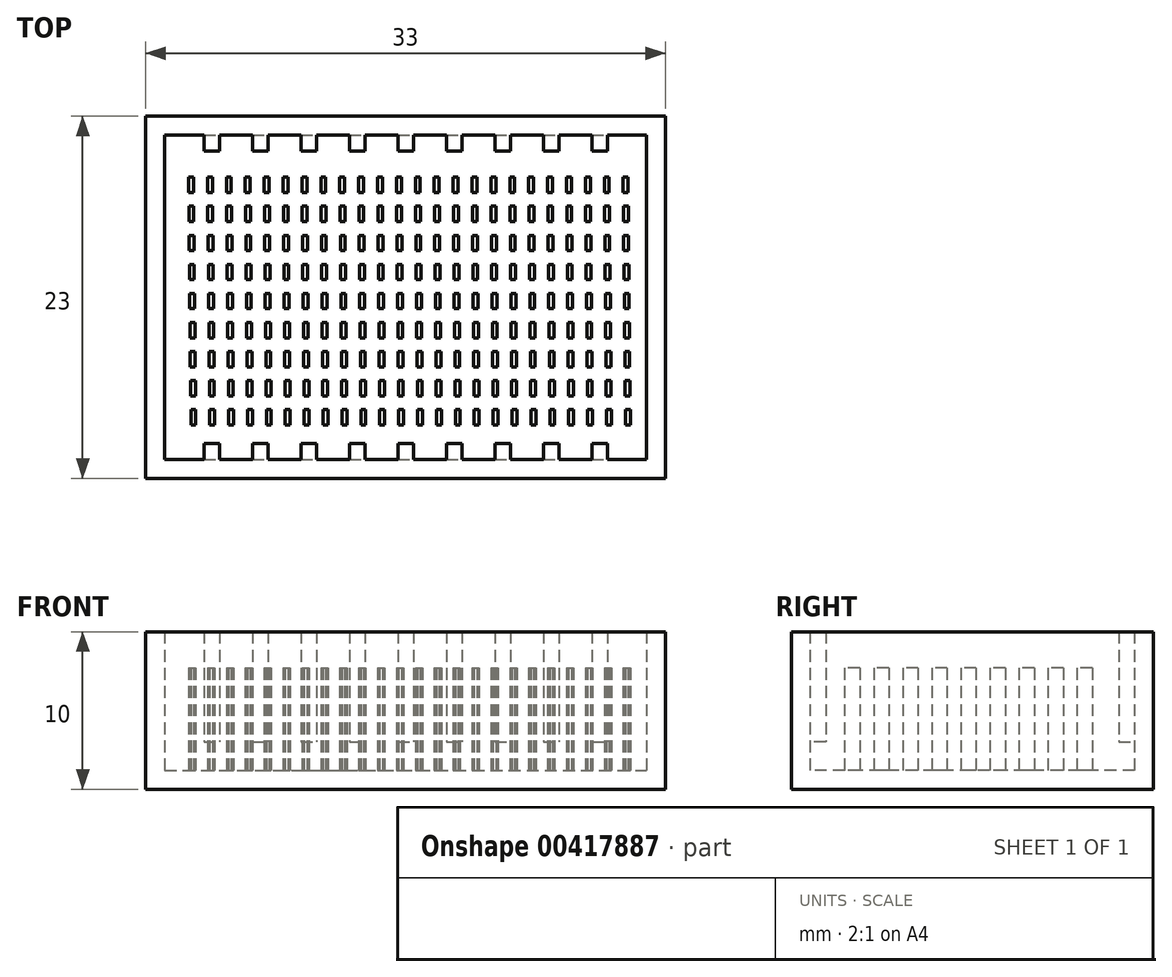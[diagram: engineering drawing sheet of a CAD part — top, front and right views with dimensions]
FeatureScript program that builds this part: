
annotation { "Feature Type Name" : "Feature", "Feature Type Description" : "" }
export const myFeature = defineFeature(function(context is Context, id is Id, definition is map)
    precondition{}
    {
        {
            var Q0;
            Q0=qCreatedBy(makeId("Top.planeOp"),FACE);
            var sketch = newSketch(context, id + "F0", { "sketchPlane" : qUnion([Q0])});
            skLineSegment(sketch, "E0.bottom", {"start": v(-104.56, 23) * mm, "end": v(-71.56, 23) * mm});
            skLineSegment(sketch, "E0.top", {"start": v(-104.56, 0) * mm, "end": v(-71.56, 0) * mm});
            skLineSegment(sketch, "E0.left", {"start": v(-104.56, 23) * mm, "end": v(-104.56, 0) * mm});
            skLineSegment(sketch, "E0.right", {"start": v(-71.56, 23) * mm, "end": v(-71.56, 0) * mm});
            skLineSegment(sketch, "E1.0", {"start": v(-103.36, 1.2) * mm, "end": v(-72.76, 1.2) * mm});
            skLineSegment(sketch, "E1.1", {"start": v(-103.36, 21.8) * mm, "end": v(-103.36, 1.2) * mm});
            skLineSegment(sketch, "E1.2", {"start": v(-103.36, 21.8) * mm, "end": v(-72.76, 21.8) * mm});
            skLineSegment(sketch, "E1.3", {"start": v(-72.76, 21.8) * mm, "end": v(-72.76, 1.2) * mm});
            skSolve(sketch);
        }
        {
            var Q0;
            Q0=makeQuery(id+"F0.imprint","IMPRINT",FACE,{"disambiguationData":[TD([[makeQuery(id+"F0.imprint","IMPRINT",EDGE,{"derivedFrom":sQuery(id+"F0.wireOp",EDGE,"E0.bottom")}),-1.0]])]});
            extrude(context, id + "F1", {"entities" : qUnion([Q0]), "depth" : 10 * mm});
        }
        {
            var Q0;
            Q0=makeQuery(id+"F0.imprint","IMPRINT",FACE,{"disambiguationData":[TD([[makeQuery(id+"F0.imprint","IMPRINT",EDGE,{"derivedFrom":sQuery(id+"F0.wireOp",EDGE,"E1.0")}),1.0]])]});
            extrude(context, id + "F2", {"entities" : qUnion([Q0]), "operationType" : NewBodyOperationType.ADD, "depth" : 1.2 * mm});
        }
        {
            var Q0;
            Q0=makeQuery(id+"F1.opExtrude","SWEPT_FACE",FACE,{"disambiguationData":[OSD([sQuery(id+"F0.wireOp",EDGE,"E1.2")])]});
            var sketch = newSketch(context, id + "F3", { "sketchPlane" : qUnion([Q0])});
            skLineSegment(sketch, "E2.bottom", {"start": v(-100.87, 10) * mm, "end": v(-99.87, 10) * mm});
            skLineSegment(sketch, "E2.top", {"start": v(-100.87, 3) * mm, "end": v(-99.87, 3) * mm});
            skLineSegment(sketch, "E2.left", {"start": v(-100.87, 10) * mm, "end": v(-100.87, 3) * mm});
            skLineSegment(sketch, "E2.right", {"start": v(-99.87, 10) * mm, "end": v(-99.87, 3) * mm});
            skLineSegment(sketch, "E3.1.0.0", {"start": v(-97.79, 10) * mm, "end": v(-96.79, 10) * mm});
            skLineSegment(sketch, "E3.1.0.1", {"start": v(-96.79, 10) * mm, "end": v(-96.79, 3) * mm});
            skLineSegment(sketch, "E3.1.0.2", {"start": v(-97.79, 10) * mm, "end": v(-97.79, 3) * mm});
            skLineSegment(sketch, "E3.1.0.3", {"start": v(-97.79, 3) * mm, "end": v(-96.79, 3) * mm});
            skLineSegment(sketch, "E3.2.0.0", {"start": v(-94.7, 10) * mm, "end": v(-93.7, 10) * mm});
            skLineSegment(sketch, "E3.2.0.1", {"start": v(-93.7, 10) * mm, "end": v(-93.7, 3) * mm});
            skLineSegment(sketch, "E3.2.0.2", {"start": v(-94.7, 10) * mm, "end": v(-94.7, 3) * mm});
            skLineSegment(sketch, "E3.2.0.3", {"start": v(-94.7, 3) * mm, "end": v(-93.7, 3) * mm});
            skLineSegment(sketch, "E3.3.0.0", {"start": v(-91.63, 10) * mm, "end": v(-90.63, 10) * mm});
            skLineSegment(sketch, "E3.3.0.1", {"start": v(-90.63, 10) * mm, "end": v(-90.63, 3) * mm});
            skLineSegment(sketch, "E3.3.0.2", {"start": v(-91.63, 10) * mm, "end": v(-91.63, 3) * mm});
            skLineSegment(sketch, "E3.3.0.3", {"start": v(-91.63, 3) * mm, "end": v(-90.63, 3) * mm});
            skLineSegment(sketch, "E3.4.0.0", {"start": v(-88.55, 10) * mm, "end": v(-87.55, 10) * mm});
            skLineSegment(sketch, "E3.4.0.1", {"start": v(-87.55, 10) * mm, "end": v(-87.55, 3) * mm});
            skLineSegment(sketch, "E3.4.0.2", {"start": v(-88.55, 10) * mm, "end": v(-88.55, 3) * mm});
            skLineSegment(sketch, "E3.4.0.3", {"start": v(-88.55, 3) * mm, "end": v(-87.55, 3) * mm});
            skLineSegment(sketch, "E3.5.0.0", {"start": v(-85.47, 10) * mm, "end": v(-84.47, 10) * mm});
            skLineSegment(sketch, "E3.5.0.1", {"start": v(-84.47, 10) * mm, "end": v(-84.47, 3) * mm});
            skLineSegment(sketch, "E3.5.0.2", {"start": v(-85.47, 10) * mm, "end": v(-85.47, 3) * mm});
            skLineSegment(sketch, "E3.5.0.3", {"start": v(-85.47, 3) * mm, "end": v(-84.47, 3) * mm});
            skLineSegment(sketch, "E3.6.0.0", {"start": v(-82.39, 10) * mm, "end": v(-81.39, 10) * mm});
            skLineSegment(sketch, "E3.6.0.1", {"start": v(-81.39, 10) * mm, "end": v(-81.39, 3) * mm});
            skLineSegment(sketch, "E3.6.0.2", {"start": v(-82.39, 10) * mm, "end": v(-82.39, 3) * mm});
            skLineSegment(sketch, "E3.6.0.3", {"start": v(-82.39, 3) * mm, "end": v(-81.39, 3) * mm});
            skLineSegment(sketch, "E3.7.0.0", {"start": v(-79.3, 10) * mm, "end": v(-78.3, 10) * mm});
            skLineSegment(sketch, "E3.7.0.1", {"start": v(-78.3, 10) * mm, "end": v(-78.3, 3) * mm});
            skLineSegment(sketch, "E3.7.0.2", {"start": v(-79.3, 10) * mm, "end": v(-79.3, 3) * mm});
            skLineSegment(sketch, "E3.7.0.3", {"start": v(-79.3, 3) * mm, "end": v(-78.3, 3) * mm});
            skLineSegment(sketch, "E3.8.0.0", {"start": v(-76.23, 10) * mm, "end": v(-75.23, 10) * mm});
            skLineSegment(sketch, "E3.8.0.1", {"start": v(-75.23, 10) * mm, "end": v(-75.23, 3) * mm});
            skLineSegment(sketch, "E3.8.0.2", {"start": v(-76.23, 10) * mm, "end": v(-76.23, 3) * mm});
            skLineSegment(sketch, "E3.8.0.3", {"start": v(-76.23, 3) * mm, "end": v(-75.23, 3) * mm});
            skLineSegment(sketch, "E3.direction1", {"start": v(-100.87, 10) * mm, "end": v(-97.79, 10) * mm, "construction": true});
            skSolve(sketch);
        }
        {
            var Q0;
            Q0=makeQuery(id+"F3.imprint","IMPRINT",FACE,{"disambiguationData":[TD([[makeQuery(id+"F3.imprint","IMPRINT",EDGE,{"derivedFrom":sQuery(id+"F3.wireOp",EDGE,"E3.1.0.0")}),-1.0]])]});
            var Q1;
            Q1=makeQuery(id+"F3.imprint","IMPRINT",FACE,{"disambiguationData":[TD([[makeQuery(id+"F3.imprint","IMPRINT",EDGE,{"derivedFrom":sQuery(id+"F3.wireOp",EDGE,"E3.2.0.0")}),-1.0]])]});
            var Q2;
            Q2=makeQuery(id+"F3.imprint","IMPRINT",FACE,{"disambiguationData":[TD([[makeQuery(id+"F3.imprint","IMPRINT",EDGE,{"derivedFrom":sQuery(id+"F3.wireOp",EDGE,"E3.3.0.0")}),-1.0]])]});
            var Q3;
            Q3=makeQuery(id+"F3.imprint","IMPRINT",FACE,{"disambiguationData":[TD([[makeQuery(id+"F3.imprint","IMPRINT",EDGE,{"derivedFrom":sQuery(id+"F3.wireOp",EDGE,"E3.4.0.0")}),-1.0]])]});
            var Q4;
            Q4=makeQuery(id+"F3.imprint","IMPRINT",FACE,{"disambiguationData":[TD([[makeQuery(id+"F3.imprint","IMPRINT",EDGE,{"derivedFrom":sQuery(id+"F3.wireOp",EDGE,"E3.5.0.0")}),-1.0]])]});
            var Q5;
            Q5=makeQuery(id+"F3.imprint","IMPRINT",FACE,{"disambiguationData":[TD([[makeQuery(id+"F3.imprint","IMPRINT",EDGE,{"derivedFrom":sQuery(id+"F3.wireOp",EDGE,"E3.6.0.0")}),-1.0]])]});
            var Q6;
            Q6=makeQuery(id+"F3.imprint","IMPRINT",FACE,{"disambiguationData":[TD([[makeQuery(id+"F3.imprint","IMPRINT",EDGE,{"derivedFrom":sQuery(id+"F3.wireOp",EDGE,"E3.7.0.0")}),-1.0]])]});
            var Q7;
            Q7=makeQuery(id+"F3.imprint","IMPRINT",FACE,{"disambiguationData":[TD([[makeQuery(id+"F3.imprint","IMPRINT",EDGE,{"derivedFrom":sQuery(id+"F3.wireOp",EDGE,"E3.8.0.0")}),-1.0]])]});
            var Q8;
            Q8=makeQuery(id+"F3.imprint","IMPRINT",FACE,{"disambiguationData":[TD([[makeQuery(id+"F3.imprint","IMPRINT",EDGE,{"derivedFrom":sQuery(id+"F3.wireOp",EDGE,"E2.bottom")}),-1.0]])]});
            extrude(context, id + "F4", {"entities" : qUnion([Q0, Q1, Q2, Q3, Q4, Q5, Q6, Q7, Q8]), "operationType" : NewBodyOperationType.ADD, "depth" : 1 * mm});
        }
        {
            var Q0;
            Q0=makeQuery(id+"F1.opExtrude","SWEPT_FACE",FACE,{"disambiguationData":[OSD([sQuery(id+"F0.wireOp",EDGE,"E1.0")])]});
            var sketch = newSketch(context, id + "F5", { "sketchPlane" : qUnion([Q0])});
            skLineSegment(sketch, "E4.0", {"start": v(76.23, 10) * mm, "end": v(75.23, 10) * mm});
            skLineSegment(sketch, "E4.1", {"start": v(76.23, 10) * mm, "end": v(76.23, 3) * mm});
            skLineSegment(sketch, "E4.2", {"start": v(75.23, 10) * mm, "end": v(75.23, 3) * mm});
            skLineSegment(sketch, "E4.3", {"start": v(76.23, 3) * mm, "end": v(75.23, 3) * mm});
            skLineSegment(sketch, "E4.4", {"start": v(79.3, 3) * mm, "end": v(78.3, 3) * mm});
            skLineSegment(sketch, "E4.5", {"start": v(79.3, 10) * mm, "end": v(79.3, 3) * mm});
            skLineSegment(sketch, "E4.6", {"start": v(78.3, 10) * mm, "end": v(78.3, 3) * mm});
            skLineSegment(sketch, "E4.7", {"start": v(79.3, 10) * mm, "end": v(78.3, 10) * mm});
            skLineSegment(sketch, "E4.8", {"start": v(82.39, 10) * mm, "end": v(81.39, 10) * mm});
            skLineSegment(sketch, "E4.9", {"start": v(81.39, 10) * mm, "end": v(81.39, 3) * mm});
            skLineSegment(sketch, "E4.10", {"start": v(82.39, 10) * mm, "end": v(82.39, 3) * mm});
            skLineSegment(sketch, "E4.11", {"start": v(82.39, 3) * mm, "end": v(81.39, 3) * mm});
            skLineSegment(sketch, "E4.12", {"start": v(85.47, 3) * mm, "end": v(84.47, 3) * mm});
            skLineSegment(sketch, "E4.13", {"start": v(85.47, 10) * mm, "end": v(85.47, 3) * mm});
            skLineSegment(sketch, "E4.14", {"start": v(84.47, 10) * mm, "end": v(84.47, 3) * mm});
            skLineSegment(sketch, "E4.15", {"start": v(85.47, 10) * mm, "end": v(84.47, 10) * mm});
            skLineSegment(sketch, "E4.16", {"start": v(87.55, 10) * mm, "end": v(87.55, 3) * mm});
            skLineSegment(sketch, "E4.17", {"start": v(88.55, 10) * mm, "end": v(88.55, 3) * mm});
            skLineSegment(sketch, "E4.18", {"start": v(88.55, 10) * mm, "end": v(87.55, 10) * mm});
            skLineSegment(sketch, "E4.19", {"start": v(88.55, 3) * mm, "end": v(87.55, 3) * mm});
            skLineSegment(sketch, "E4.20", {"start": v(91.63, 3) * mm, "end": v(90.63, 3) * mm});
            skLineSegment(sketch, "E4.21", {"start": v(90.63, 10) * mm, "end": v(90.63, 3) * mm});
            skLineSegment(sketch, "E4.22", {"start": v(91.63, 10) * mm, "end": v(91.63, 3) * mm});
            skLineSegment(sketch, "E4.23", {"start": v(91.63, 10) * mm, "end": v(90.63, 10) * mm});
            skLineSegment(sketch, "E4.24", {"start": v(94.7, 10) * mm, "end": v(93.7, 10) * mm});
            skLineSegment(sketch, "E4.25", {"start": v(93.7, 10) * mm, "end": v(93.7, 3) * mm});
            skLineSegment(sketch, "E4.26", {"start": v(94.7, 10) * mm, "end": v(94.7, 3) * mm});
            skLineSegment(sketch, "E4.27", {"start": v(94.7, 3) * mm, "end": v(93.7, 3) * mm});
            skLineSegment(sketch, "E4.28", {"start": v(96.79, 10) * mm, "end": v(96.79, 3) * mm});
            skLineSegment(sketch, "E4.29", {"start": v(97.79, 10) * mm, "end": v(97.79, 3) * mm});
            skLineSegment(sketch, "E4.30", {"start": v(97.79, 10) * mm, "end": v(96.79, 10) * mm});
            skLineSegment(sketch, "E4.31", {"start": v(97.79, 3) * mm, "end": v(96.79, 3) * mm});
            skLineSegment(sketch, "E4.32", {"start": v(100.87, 3) * mm, "end": v(99.87, 3) * mm});
            skLineSegment(sketch, "E4.33", {"start": v(100.87, 10) * mm, "end": v(100.87, 3) * mm});
            skLineSegment(sketch, "E4.34", {"start": v(99.87, 10) * mm, "end": v(99.87, 3) * mm});
            skLineSegment(sketch, "E4.35", {"start": v(100.87, 10) * mm, "end": v(99.87, 10) * mm});
            skSolve(sketch);
        }
        {
            var Q0;
            Q0=makeQuery(id+"F5.imprint","IMPRINT",FACE,{"disambiguationData":[TD([[makeQuery(id+"F5.imprint","IMPRINT",EDGE,{"derivedFrom":sQuery(id+"F5.wireOp",EDGE,"E4.0")}),1.0]])]});
            var Q1;
            Q1=makeQuery(id+"F5.imprint","IMPRINT",FACE,{"disambiguationData":[TD([[makeQuery(id+"F5.imprint","IMPRINT",EDGE,{"derivedFrom":sQuery(id+"F5.wireOp",EDGE,"E4.4")}),-1.0]])]});
            var Q2;
            Q2=makeQuery(id+"F5.imprint","IMPRINT",FACE,{"disambiguationData":[TD([[makeQuery(id+"F5.imprint","IMPRINT",EDGE,{"derivedFrom":sQuery(id+"F5.wireOp",EDGE,"E4.8")}),1.0]])]});
            var Q3;
            Q3=makeQuery(id+"F5.imprint","IMPRINT",FACE,{"disambiguationData":[TD([[makeQuery(id+"F5.imprint","IMPRINT",EDGE,{"derivedFrom":sQuery(id+"F5.wireOp",EDGE,"E4.12")}),-1.0]])]});
            var Q4;
            Q4=makeQuery(id+"F5.imprint","IMPRINT",FACE,{"disambiguationData":[TD([[makeQuery(id+"F5.imprint","IMPRINT",EDGE,{"derivedFrom":sQuery(id+"F5.wireOp",EDGE,"E4.16")}),1.0]])]});
            var Q5;
            Q5=makeQuery(id+"F5.imprint","IMPRINT",FACE,{"disambiguationData":[TD([[makeQuery(id+"F5.imprint","IMPRINT",EDGE,{"derivedFrom":sQuery(id+"F5.wireOp",EDGE,"E4.20")}),-1.0]])]});
            var Q6;
            Q6=makeQuery(id+"F5.imprint","IMPRINT",FACE,{"disambiguationData":[TD([[makeQuery(id+"F5.imprint","IMPRINT",EDGE,{"derivedFrom":sQuery(id+"F5.wireOp",EDGE,"E4.24")}),1.0]])]});
            var Q7;
            Q7=makeQuery(id+"F5.imprint","IMPRINT",FACE,{"disambiguationData":[TD([[makeQuery(id+"F5.imprint","IMPRINT",EDGE,{"derivedFrom":sQuery(id+"F5.wireOp",EDGE,"E4.28")}),1.0]])]});
            var Q8;
            Q8=makeQuery(id+"F5.imprint","IMPRINT",FACE,{"disambiguationData":[TD([[makeQuery(id+"F5.imprint","IMPRINT",EDGE,{"derivedFrom":sQuery(id+"F5.wireOp",EDGE,"E4.32")}),-1.0]])]});
            extrude(context, id + "F6", {"entities" : qUnion([Q0, Q1, Q2, Q3, Q4, Q5, Q6, Q7, Q8]), "operationType" : NewBodyOperationType.ADD, "depth" : 1 * mm});
        }
        {
            var Q0;
            Q0=makeQuery(id+"F2.opExtrude","CAP_FACE",FACE,{"disambiguationData":[OSD([sQuery(id+"F0.wireOp",EDGE,"E1.0"),sQuery(id+"F0.wireOp",EDGE,"E1.1"),sQuery(id+"F0.wireOp",EDGE,"E1.2"),sQuery(id+"F0.wireOp",EDGE,"E1.3")])],"isStart":false});
            var sketch = newSketch(context, id + "F7", { "sketchPlane" : qUnion([Q0])});
            skLineSegment(sketch, "E5.bottom", {"start": v(-101.84, 19.12) * mm, "end": v(-101.53, 19.12) * mm});
            skLineSegment(sketch, "E5.top", {"start": v(-101.84, 18.16) * mm, "end": v(-101.53, 18.16) * mm});
            skLineSegment(sketch, "E5.left", {"start": v(-101.84, 19.12) * mm, "end": v(-101.84, 18.16) * mm});
            skLineSegment(sketch, "E5.right", {"start": v(-101.53, 19.12) * mm, "end": v(-101.53, 18.16) * mm});
            skLineSegment(sketch, "E6.1.0.0", {"start": v(-100.64, 19.12) * mm, "end": v(-100.33, 19.12) * mm});
            skLineSegment(sketch, "E6.1.0.1", {"start": v(-100.64, 18.16) * mm, "end": v(-100.33, 18.16) * mm});
            skLineSegment(sketch, "E6.1.0.2", {"start": v(-100.64, 19.12) * mm, "end": v(-100.64, 18.16) * mm});
            skLineSegment(sketch, "E6.1.0.3", {"start": v(-100.33, 19.12) * mm, "end": v(-100.33, 18.16) * mm});
            skLineSegment(sketch, "E6.2.0.0", {"start": v(-99.44, 19.12) * mm, "end": v(-99.13, 19.12) * mm});
            skLineSegment(sketch, "E6.2.0.1", {"start": v(-99.44, 18.16) * mm, "end": v(-99.13, 18.16) * mm});
            skLineSegment(sketch, "E6.2.0.2", {"start": v(-99.44, 19.12) * mm, "end": v(-99.44, 18.16) * mm});
            skLineSegment(sketch, "E6.2.0.3", {"start": v(-99.13, 19.12) * mm, "end": v(-99.13, 18.16) * mm});
            skLineSegment(sketch, "E6.3.0.0", {"start": v(-98.24, 19.12) * mm, "end": v(-97.93, 19.12) * mm});
            skLineSegment(sketch, "E6.3.0.1", {"start": v(-98.24, 18.16) * mm, "end": v(-97.93, 18.16) * mm});
            skLineSegment(sketch, "E6.3.0.2", {"start": v(-98.24, 19.12) * mm, "end": v(-98.24, 18.16) * mm});
            skLineSegment(sketch, "E6.3.0.3", {"start": v(-97.93, 19.12) * mm, "end": v(-97.93, 18.16) * mm});
            skLineSegment(sketch, "E6.4.0.0", {"start": v(-97.04, 19.12) * mm, "end": v(-96.73, 19.12) * mm});
            skLineSegment(sketch, "E6.4.0.1", {"start": v(-97.04, 18.16) * mm, "end": v(-96.73, 18.16) * mm});
            skLineSegment(sketch, "E6.4.0.2", {"start": v(-97.04, 19.12) * mm, "end": v(-97.04, 18.16) * mm});
            skLineSegment(sketch, "E6.4.0.3", {"start": v(-96.73, 19.12) * mm, "end": v(-96.73, 18.16) * mm});
            skLineSegment(sketch, "E6.5.0.0", {"start": v(-95.84, 19.12) * mm, "end": v(-95.53, 19.12) * mm});
            skLineSegment(sketch, "E6.5.0.1", {"start": v(-95.84, 18.16) * mm, "end": v(-95.53, 18.16) * mm});
            skLineSegment(sketch, "E6.5.0.2", {"start": v(-95.84, 19.12) * mm, "end": v(-95.84, 18.16) * mm});
            skLineSegment(sketch, "E6.5.0.3", {"start": v(-95.53, 19.12) * mm, "end": v(-95.53, 18.16) * mm});
            skLineSegment(sketch, "E6.6.0.0", {"start": v(-94.64, 19.12) * mm, "end": v(-94.33, 19.12) * mm});
            skLineSegment(sketch, "E6.6.0.1", {"start": v(-94.64, 18.16) * mm, "end": v(-94.33, 18.16) * mm});
            skLineSegment(sketch, "E6.6.0.2", {"start": v(-94.64, 19.12) * mm, "end": v(-94.64, 18.16) * mm});
            skLineSegment(sketch, "E6.6.0.3", {"start": v(-94.33, 19.12) * mm, "end": v(-94.33, 18.16) * mm});
            skLineSegment(sketch, "E6.7.0.0", {"start": v(-93.44, 19.12) * mm, "end": v(-93.13, 19.12) * mm});
            skLineSegment(sketch, "E6.7.0.1", {"start": v(-93.44, 18.16) * mm, "end": v(-93.13, 18.16) * mm});
            skLineSegment(sketch, "E6.7.0.2", {"start": v(-93.44, 19.12) * mm, "end": v(-93.44, 18.16) * mm});
            skLineSegment(sketch, "E6.7.0.3", {"start": v(-93.13, 19.12) * mm, "end": v(-93.13, 18.16) * mm});
            skLineSegment(sketch, "E6.8.0.0", {"start": v(-92.24, 19.12) * mm, "end": v(-91.93, 19.12) * mm});
            skLineSegment(sketch, "E6.8.0.1", {"start": v(-92.24, 18.16) * mm, "end": v(-91.93, 18.16) * mm});
            skLineSegment(sketch, "E6.8.0.2", {"start": v(-92.24, 19.12) * mm, "end": v(-92.24, 18.16) * mm});
            skLineSegment(sketch, "E6.8.0.3", {"start": v(-91.93, 19.12) * mm, "end": v(-91.93, 18.16) * mm});
            skLineSegment(sketch, "E6.9.0.0", {"start": v(-91.04, 19.12) * mm, "end": v(-90.73, 19.12) * mm});
            skLineSegment(sketch, "E6.9.0.1", {"start": v(-91.04, 18.16) * mm, "end": v(-90.73, 18.16) * mm});
            skLineSegment(sketch, "E6.9.0.2", {"start": v(-91.04, 19.12) * mm, "end": v(-91.04, 18.16) * mm});
            skLineSegment(sketch, "E6.9.0.3", {"start": v(-90.73, 19.12) * mm, "end": v(-90.73, 18.16) * mm});
            skLineSegment(sketch, "E6.10.0.0", {"start": v(-89.84, 19.12) * mm, "end": v(-89.53, 19.12) * mm});
            skLineSegment(sketch, "E6.10.0.1", {"start": v(-89.84, 18.16) * mm, "end": v(-89.53, 18.16) * mm});
            skLineSegment(sketch, "E6.10.0.2", {"start": v(-89.84, 19.12) * mm, "end": v(-89.84, 18.16) * mm});
            skLineSegment(sketch, "E6.10.0.3", {"start": v(-89.53, 19.12) * mm, "end": v(-89.53, 18.16) * mm});
            skLineSegment(sketch, "E6.11.0.0", {"start": v(-88.64, 19.12) * mm, "end": v(-88.33, 19.12) * mm});
            skLineSegment(sketch, "E6.11.0.1", {"start": v(-88.64, 18.16) * mm, "end": v(-88.33, 18.16) * mm});
            skLineSegment(sketch, "E6.11.0.2", {"start": v(-88.64, 19.12) * mm, "end": v(-88.64, 18.16) * mm});
            skLineSegment(sketch, "E6.11.0.3", {"start": v(-88.33, 19.12) * mm, "end": v(-88.33, 18.16) * mm});
            skLineSegment(sketch, "E6.12.0.0", {"start": v(-87.44, 19.12) * mm, "end": v(-87.13, 19.12) * mm});
            skLineSegment(sketch, "E6.12.0.1", {"start": v(-87.44, 18.16) * mm, "end": v(-87.13, 18.16) * mm});
            skLineSegment(sketch, "E6.12.0.2", {"start": v(-87.44, 19.12) * mm, "end": v(-87.44, 18.16) * mm});
            skLineSegment(sketch, "E6.12.0.3", {"start": v(-87.13, 19.12) * mm, "end": v(-87.13, 18.16) * mm});
            skLineSegment(sketch, "E6.13.0.0", {"start": v(-86.24, 19.12) * mm, "end": v(-85.93, 19.12) * mm});
            skLineSegment(sketch, "E6.13.0.1", {"start": v(-86.24, 18.16) * mm, "end": v(-85.93, 18.16) * mm});
            skLineSegment(sketch, "E6.13.0.2", {"start": v(-86.24, 19.12) * mm, "end": v(-86.24, 18.16) * mm});
            skLineSegment(sketch, "E6.13.0.3", {"start": v(-85.93, 19.12) * mm, "end": v(-85.93, 18.16) * mm});
            skLineSegment(sketch, "E6.14.0.0", {"start": v(-85.04, 19.12) * mm, "end": v(-84.73, 19.12) * mm});
            skLineSegment(sketch, "E6.14.0.1", {"start": v(-85.04, 18.16) * mm, "end": v(-84.73, 18.16) * mm});
            skLineSegment(sketch, "E6.14.0.2", {"start": v(-85.04, 19.12) * mm, "end": v(-85.04, 18.16) * mm});
            skLineSegment(sketch, "E6.14.0.3", {"start": v(-84.73, 19.12) * mm, "end": v(-84.73, 18.16) * mm});
            skLineSegment(sketch, "E6.15.0.0", {"start": v(-83.84, 19.12) * mm, "end": v(-83.53, 19.12) * mm});
            skLineSegment(sketch, "E6.15.0.1", {"start": v(-83.84, 18.16) * mm, "end": v(-83.53, 18.16) * mm});
            skLineSegment(sketch, "E6.15.0.2", {"start": v(-83.84, 19.12) * mm, "end": v(-83.84, 18.16) * mm});
            skLineSegment(sketch, "E6.15.0.3", {"start": v(-83.53, 19.12) * mm, "end": v(-83.53, 18.16) * mm});
            skLineSegment(sketch, "E6.16.0.0", {"start": v(-82.64, 19.12) * mm, "end": v(-82.33, 19.12) * mm});
            skLineSegment(sketch, "E6.16.0.1", {"start": v(-82.64, 18.16) * mm, "end": v(-82.33, 18.16) * mm});
            skLineSegment(sketch, "E6.16.0.2", {"start": v(-82.64, 19.12) * mm, "end": v(-82.64, 18.16) * mm});
            skLineSegment(sketch, "E6.16.0.3", {"start": v(-82.33, 19.12) * mm, "end": v(-82.33, 18.16) * mm});
            skLineSegment(sketch, "E6.17.0.0", {"start": v(-81.44, 19.12) * mm, "end": v(-81.13, 19.12) * mm});
            skLineSegment(sketch, "E6.17.0.1", {"start": v(-81.44, 18.16) * mm, "end": v(-81.13, 18.16) * mm});
            skLineSegment(sketch, "E6.17.0.2", {"start": v(-81.44, 19.12) * mm, "end": v(-81.44, 18.16) * mm});
            skLineSegment(sketch, "E6.17.0.3", {"start": v(-81.13, 19.12) * mm, "end": v(-81.13, 18.16) * mm});
            skLineSegment(sketch, "E6.18.0.0", {"start": v(-80.24, 19.12) * mm, "end": v(-79.93, 19.12) * mm});
            skLineSegment(sketch, "E6.18.0.1", {"start": v(-80.24, 18.16) * mm, "end": v(-79.93, 18.16) * mm});
            skLineSegment(sketch, "E6.18.0.2", {"start": v(-80.24, 19.12) * mm, "end": v(-80.24, 18.16) * mm});
            skLineSegment(sketch, "E6.18.0.3", {"start": v(-79.93, 19.12) * mm, "end": v(-79.93, 18.16) * mm});
            skLineSegment(sketch, "E6.19.0.0", {"start": v(-79.04, 19.12) * mm, "end": v(-78.73, 19.12) * mm});
            skLineSegment(sketch, "E6.19.0.1", {"start": v(-79.04, 18.16) * mm, "end": v(-78.73, 18.16) * mm});
            skLineSegment(sketch, "E6.19.0.2", {"start": v(-79.04, 19.12) * mm, "end": v(-79.04, 18.16) * mm});
            skLineSegment(sketch, "E6.19.0.3", {"start": v(-78.73, 19.12) * mm, "end": v(-78.73, 18.16) * mm});
            skLineSegment(sketch, "E6.20.0.0", {"start": v(-77.84, 19.12) * mm, "end": v(-77.53, 19.12) * mm});
            skLineSegment(sketch, "E6.20.0.1", {"start": v(-77.84, 18.16) * mm, "end": v(-77.53, 18.16) * mm});
            skLineSegment(sketch, "E6.20.0.2", {"start": v(-77.84, 19.12) * mm, "end": v(-77.84, 18.16) * mm});
            skLineSegment(sketch, "E6.20.0.3", {"start": v(-77.53, 19.12) * mm, "end": v(-77.53, 18.16) * mm});
            skLineSegment(sketch, "E6.21.0.0", {"start": v(-76.64, 19.12) * mm, "end": v(-76.33, 19.12) * mm});
            skLineSegment(sketch, "E6.21.0.1", {"start": v(-76.64, 18.16) * mm, "end": v(-76.33, 18.16) * mm});
            skLineSegment(sketch, "E6.21.0.2", {"start": v(-76.64, 19.12) * mm, "end": v(-76.64, 18.16) * mm});
            skLineSegment(sketch, "E6.21.0.3", {"start": v(-76.33, 19.12) * mm, "end": v(-76.33, 18.16) * mm});
            skLineSegment(sketch, "E6.22.0.0", {"start": v(-75.44, 19.12) * mm, "end": v(-75.13, 19.12) * mm});
            skLineSegment(sketch, "E6.22.0.1", {"start": v(-75.44, 18.16) * mm, "end": v(-75.13, 18.16) * mm});
            skLineSegment(sketch, "E6.22.0.2", {"start": v(-75.44, 19.12) * mm, "end": v(-75.44, 18.16) * mm});
            skLineSegment(sketch, "E6.22.0.3", {"start": v(-75.13, 19.12) * mm, "end": v(-75.13, 18.16) * mm});
            skLineSegment(sketch, "E6.23.0.0", {"start": v(-74.24, 19.12) * mm, "end": v(-73.93, 19.12) * mm});
            skLineSegment(sketch, "E6.23.0.1", {"start": v(-74.24, 18.16) * mm, "end": v(-73.93, 18.16) * mm});
            skLineSegment(sketch, "E6.23.0.2", {"start": v(-74.24, 19.12) * mm, "end": v(-74.24, 18.16) * mm});
            skLineSegment(sketch, "E6.23.0.3", {"start": v(-73.93, 19.12) * mm, "end": v(-73.93, 18.16) * mm});
            skLineSegment(sketch, "E6.direction1", {"start": v(-101.84, 18.16) * mm, "end": v(-100.64, 18.16) * mm, "construction": true});
            skLineSegment(sketch, "E7.1.0.0", {"start": v(-101.82, 17.28) * mm, "end": v(-101.82, 16.31) * mm});
            skLineSegment(sketch, "E7.1.0.1", {"start": v(-101.5, 17.28) * mm, "end": v(-101.5, 16.31) * mm});
            skLineSegment(sketch, "E7.1.0.2", {"start": v(-99.42, 17.28) * mm, "end": v(-99.42, 16.31) * mm});
            skLineSegment(sketch, "E7.1.0.3", {"start": v(-99.1, 17.28) * mm, "end": v(-99.1, 16.31) * mm});
            skLineSegment(sketch, "E7.1.0.4", {"start": v(-75.42, 17.28) * mm, "end": v(-75.1, 17.28) * mm});
            skLineSegment(sketch, "E7.1.0.5", {"start": v(-80.22, 17.28) * mm, "end": v(-79.9, 17.28) * mm});
            skLineSegment(sketch, "E7.1.0.6", {"start": v(-85.02, 17.28) * mm, "end": v(-84.7, 17.28) * mm});
            skLineSegment(sketch, "E7.1.0.7", {"start": v(-82.62, 17.28) * mm, "end": v(-82.62, 16.31) * mm});
            skLineSegment(sketch, "E7.1.0.8", {"start": v(-87.42, 17.28) * mm, "end": v(-87.42, 16.31) * mm});
            skLineSegment(sketch, "E7.1.0.9", {"start": v(-92.22, 17.28) * mm, "end": v(-92.22, 16.31) * mm});
            skLineSegment(sketch, "E7.1.0.10", {"start": v(-97.02, 17.28) * mm, "end": v(-97.02, 16.31) * mm});
            skLineSegment(sketch, "E7.1.0.11", {"start": v(-77.82, 17.28) * mm, "end": v(-77.82, 16.31) * mm});
            skLineSegment(sketch, "E7.1.0.12", {"start": v(-85.02, 16.31) * mm, "end": v(-84.7, 16.31) * mm});
            skLineSegment(sketch, "E7.1.0.13", {"start": v(-77.5, 17.28) * mm, "end": v(-77.5, 16.31) * mm});
            skLineSegment(sketch, "E7.1.0.14", {"start": v(-89.82, 17.28) * mm, "end": v(-89.82, 16.31) * mm});
            skLineSegment(sketch, "E7.1.0.15", {"start": v(-94.62, 17.28) * mm, "end": v(-94.62, 16.31) * mm});
            skLineSegment(sketch, "E7.1.0.16", {"start": v(-75.42, 17.28) * mm, "end": v(-75.42, 16.31) * mm});
            skLineSegment(sketch, "E7.1.0.17", {"start": v(-80.22, 17.28) * mm, "end": v(-80.22, 16.31) * mm});
            skLineSegment(sketch, "E7.1.0.18", {"start": v(-85.02, 17.28) * mm, "end": v(-85.02, 16.31) * mm});
            skLineSegment(sketch, "E7.1.0.19", {"start": v(-82.3, 17.28) * mm, "end": v(-82.3, 16.31) * mm});
            skLineSegment(sketch, "E7.1.0.20", {"start": v(-87.1, 17.28) * mm, "end": v(-87.1, 16.31) * mm});
            skLineSegment(sketch, "E7.1.0.21", {"start": v(-91.9, 17.28) * mm, "end": v(-91.9, 16.31) * mm});
            skLineSegment(sketch, "E7.1.0.22", {"start": v(-96.7, 17.28) * mm, "end": v(-96.7, 16.31) * mm});
            skLineSegment(sketch, "E7.1.0.23", {"start": v(-89.5, 17.28) * mm, "end": v(-89.5, 16.31) * mm});
            skLineSegment(sketch, "E7.1.0.24", {"start": v(-94.3, 17.28) * mm, "end": v(-94.3, 16.31) * mm});
            skLineSegment(sketch, "E7.1.0.25", {"start": v(-75.1, 17.28) * mm, "end": v(-75.1, 16.31) * mm});
            skLineSegment(sketch, "E7.1.0.26", {"start": v(-79.9, 17.28) * mm, "end": v(-79.9, 16.31) * mm});
            skLineSegment(sketch, "E7.1.0.27", {"start": v(-84.7, 17.28) * mm, "end": v(-84.7, 16.31) * mm});
            skLineSegment(sketch, "E7.1.0.28", {"start": v(-83.82, 16.31) * mm, "end": v(-83.5, 16.31) * mm});
            skLineSegment(sketch, "E7.1.0.29", {"start": v(-74.22, 16.31) * mm, "end": v(-73.9, 16.31) * mm});
            skLineSegment(sketch, "E7.1.0.30", {"start": v(-79.02, 16.31) * mm, "end": v(-78.7, 16.31) * mm});
            skLineSegment(sketch, "E7.1.0.31", {"start": v(-83.82, 17.28) * mm, "end": v(-83.82, 16.31) * mm});
            skLineSegment(sketch, "E7.1.0.32", {"start": v(-81.42, 16.31) * mm, "end": v(-81.1, 16.31) * mm});
            skLineSegment(sketch, "E7.1.0.33", {"start": v(-74.22, 17.28) * mm, "end": v(-74.22, 16.31) * mm});
            skLineSegment(sketch, "E7.1.0.34", {"start": v(-79.02, 17.28) * mm, "end": v(-79.02, 16.31) * mm});
            skLineSegment(sketch, "E7.1.0.35", {"start": v(-76.62, 16.31) * mm, "end": v(-76.3, 16.31) * mm});
            skLineSegment(sketch, "E7.1.0.36", {"start": v(-81.42, 17.28) * mm, "end": v(-81.42, 16.31) * mm});
            skLineSegment(sketch, "E7.1.0.37", {"start": v(-83.5, 17.28) * mm, "end": v(-83.5, 16.31) * mm});
            skLineSegment(sketch, "E7.1.0.38", {"start": v(-73.9, 17.28) * mm, "end": v(-73.9, 16.31) * mm});
            skLineSegment(sketch, "E7.1.0.39", {"start": v(-78.7, 17.28) * mm, "end": v(-78.7, 16.31) * mm});
            skLineSegment(sketch, "E7.1.0.40", {"start": v(-76.62, 17.28) * mm, "end": v(-76.62, 16.31) * mm});
            skLineSegment(sketch, "E7.1.0.41", {"start": v(-82.62, 17.28) * mm, "end": v(-82.3, 17.28) * mm});
            skLineSegment(sketch, "E7.1.0.42", {"start": v(-87.42, 17.28) * mm, "end": v(-87.1, 17.28) * mm});
            skLineSegment(sketch, "E7.1.0.43", {"start": v(-92.22, 17.28) * mm, "end": v(-91.9, 17.28) * mm});
            skLineSegment(sketch, "E7.1.0.44", {"start": v(-97.02, 17.28) * mm, "end": v(-96.7, 17.28) * mm});
            skLineSegment(sketch, "E7.1.0.45", {"start": v(-101.82, 16.31) * mm, "end": v(-100.62, 16.31) * mm, "construction": true});
            skLineSegment(sketch, "E7.1.0.46", {"start": v(-77.82, 17.28) * mm, "end": v(-77.5, 17.28) * mm});
            skLineSegment(sketch, "E7.1.0.47", {"start": v(-76.3, 17.28) * mm, "end": v(-76.3, 16.31) * mm});
            skLineSegment(sketch, "E7.1.0.48", {"start": v(-81.1, 17.28) * mm, "end": v(-81.1, 16.31) * mm});
            skLineSegment(sketch, "E7.1.0.49", {"start": v(-98.22, 16.31) * mm, "end": v(-97.9, 16.31) * mm});
            skLineSegment(sketch, "E7.1.0.50", {"start": v(-97.02, 16.31) * mm, "end": v(-96.7, 16.31) * mm});
            skLineSegment(sketch, "E7.1.0.51", {"start": v(-92.22, 16.31) * mm, "end": v(-91.9, 16.31) * mm});
            skLineSegment(sketch, "E7.1.0.52", {"start": v(-87.42, 16.31) * mm, "end": v(-87.1, 16.31) * mm});
            skLineSegment(sketch, "E7.1.0.53", {"start": v(-82.62, 16.31) * mm, "end": v(-82.3, 16.31) * mm});
            skLineSegment(sketch, "E7.1.0.54", {"start": v(-77.82, 16.31) * mm, "end": v(-77.5, 16.31) * mm});
            skLineSegment(sketch, "E7.1.0.55", {"start": v(-98.22, 17.28) * mm, "end": v(-98.22, 16.31) * mm});
            skLineSegment(sketch, "E7.1.0.56", {"start": v(-97.9, 17.28) * mm, "end": v(-97.9, 16.31) * mm});
            skLineSegment(sketch, "E7.1.0.57", {"start": v(-101.82, 17.28) * mm, "end": v(-101.5, 17.28) * mm});
            skLineSegment(sketch, "E7.1.0.58", {"start": v(-101.82, 16.31) * mm, "end": v(-101.5, 16.31) * mm});
            skLineSegment(sketch, "E7.1.0.59", {"start": v(-100.62, 17.28) * mm, "end": v(-100.3, 17.28) * mm});
            skLineSegment(sketch, "E7.1.0.60", {"start": v(-100.62, 16.31) * mm, "end": v(-100.3, 16.31) * mm});
            skLineSegment(sketch, "E7.1.0.61", {"start": v(-100.62, 17.28) * mm, "end": v(-100.62, 16.31) * mm});
            skLineSegment(sketch, "E7.1.0.62", {"start": v(-100.3, 17.28) * mm, "end": v(-100.3, 16.31) * mm});
            skLineSegment(sketch, "E7.1.0.63", {"start": v(-99.42, 17.28) * mm, "end": v(-99.1, 17.28) * mm});
            skLineSegment(sketch, "E7.1.0.64", {"start": v(-99.42, 16.31) * mm, "end": v(-99.1, 16.31) * mm});
            skLineSegment(sketch, "E7.1.0.65", {"start": v(-98.22, 17.28) * mm, "end": v(-97.9, 17.28) * mm});
            skLineSegment(sketch, "E7.1.0.66", {"start": v(-89.82, 17.28) * mm, "end": v(-89.5, 17.28) * mm});
            skLineSegment(sketch, "E7.1.0.67", {"start": v(-94.62, 17.28) * mm, "end": v(-94.3, 17.28) * mm});
            skLineSegment(sketch, "E7.1.0.68", {"start": v(-89.82, 16.31) * mm, "end": v(-89.5, 16.31) * mm});
            skLineSegment(sketch, "E7.1.0.69", {"start": v(-94.62, 16.31) * mm, "end": v(-94.3, 16.31) * mm});
            skLineSegment(sketch, "E7.1.0.70", {"start": v(-75.42, 16.31) * mm, "end": v(-75.1, 16.31) * mm});
            skLineSegment(sketch, "E7.1.0.71", {"start": v(-80.22, 16.31) * mm, "end": v(-79.9, 16.31) * mm});
            skLineSegment(sketch, "E7.1.0.72", {"start": v(-81.42, 17.28) * mm, "end": v(-81.1, 17.28) * mm});
            skLineSegment(sketch, "E7.1.0.73", {"start": v(-88.62, 16.31) * mm, "end": v(-88.3, 16.31) * mm});
            skLineSegment(sketch, "E7.1.0.74", {"start": v(-86.22, 17.28) * mm, "end": v(-85.9, 17.28) * mm});
            skLineSegment(sketch, "E7.1.0.75", {"start": v(-91.02, 17.28) * mm, "end": v(-90.7, 17.28) * mm});
            skLineSegment(sketch, "E7.1.0.76", {"start": v(-93.42, 16.31) * mm, "end": v(-93.1, 16.31) * mm});
            skLineSegment(sketch, "E7.1.0.77", {"start": v(-95.82, 17.28) * mm, "end": v(-95.5, 17.28) * mm});
            skLineSegment(sketch, "E7.1.0.78", {"start": v(-76.62, 17.28) * mm, "end": v(-76.3, 17.28) * mm});
            skLineSegment(sketch, "E7.1.0.79", {"start": v(-88.62, 17.28) * mm, "end": v(-88.3, 17.28) * mm});
            skLineSegment(sketch, "E7.1.0.80", {"start": v(-93.42, 17.28) * mm, "end": v(-93.1, 17.28) * mm});
            skLineSegment(sketch, "E7.1.0.81", {"start": v(-74.22, 17.28) * mm, "end": v(-73.9, 17.28) * mm});
            skLineSegment(sketch, "E7.1.0.82", {"start": v(-79.02, 17.28) * mm, "end": v(-78.7, 17.28) * mm});
            skLineSegment(sketch, "E7.1.0.83", {"start": v(-83.82, 17.28) * mm, "end": v(-83.5, 17.28) * mm});
            skLineSegment(sketch, "E7.1.0.84", {"start": v(-86.22, 16.31) * mm, "end": v(-85.9, 16.31) * mm});
            skLineSegment(sketch, "E7.1.0.85", {"start": v(-88.62, 17.28) * mm, "end": v(-88.62, 16.31) * mm});
            skLineSegment(sketch, "E7.1.0.86", {"start": v(-91.02, 16.31) * mm, "end": v(-90.7, 16.31) * mm});
            skLineSegment(sketch, "E7.1.0.87", {"start": v(-93.42, 17.28) * mm, "end": v(-93.42, 16.31) * mm});
            skLineSegment(sketch, "E7.1.0.88", {"start": v(-95.82, 16.31) * mm, "end": v(-95.5, 16.31) * mm});
            skLineSegment(sketch, "E7.1.0.89", {"start": v(-88.3, 17.28) * mm, "end": v(-88.3, 16.31) * mm});
            skLineSegment(sketch, "E7.1.0.90", {"start": v(-86.22, 17.28) * mm, "end": v(-86.22, 16.31) * mm});
            skLineSegment(sketch, "E7.1.0.91", {"start": v(-93.1, 17.28) * mm, "end": v(-93.1, 16.31) * mm});
            skLineSegment(sketch, "E7.1.0.92", {"start": v(-91.02, 17.28) * mm, "end": v(-91.02, 16.31) * mm});
            skLineSegment(sketch, "E7.1.0.93", {"start": v(-95.82, 17.28) * mm, "end": v(-95.82, 16.31) * mm});
            skLineSegment(sketch, "E7.1.0.94", {"start": v(-90.7, 17.28) * mm, "end": v(-90.7, 16.31) * mm});
            skLineSegment(sketch, "E7.1.0.95", {"start": v(-95.5, 17.28) * mm, "end": v(-95.5, 16.31) * mm});
            skLineSegment(sketch, "E7.1.0.96", {"start": v(-85.9, 17.28) * mm, "end": v(-85.9, 16.31) * mm});
            skLineSegment(sketch, "E7.2.0.0", {"start": v(-101.8, 15.43) * mm, "end": v(-101.8, 14.46) * mm});
            skLineSegment(sketch, "E7.2.0.1", {"start": v(-101.5, 15.43) * mm, "end": v(-101.5, 14.46) * mm});
            skLineSegment(sketch, "E7.2.0.2", {"start": v(-99.4, 15.43) * mm, "end": v(-99.4, 14.46) * mm});
            skLineSegment(sketch, "E7.2.0.3", {"start": v(-99.1, 15.43) * mm, "end": v(-99.1, 14.46) * mm});
            skLineSegment(sketch, "E7.2.0.4", {"start": v(-75.4, 15.43) * mm, "end": v(-75.1, 15.43) * mm});
            skLineSegment(sketch, "E7.2.0.5", {"start": v(-80.2, 15.43) * mm, "end": v(-79.9, 15.43) * mm});
            skLineSegment(sketch, "E7.2.0.6", {"start": v(-85, 15.43) * mm, "end": v(-84.7, 15.43) * mm});
            skLineSegment(sketch, "E7.2.0.7", {"start": v(-82.6, 15.43) * mm, "end": v(-82.6, 14.46) * mm});
            skLineSegment(sketch, "E7.2.0.8", {"start": v(-87.4, 15.43) * mm, "end": v(-87.4, 14.46) * mm});
            skLineSegment(sketch, "E7.2.0.9", {"start": v(-92.2, 15.43) * mm, "end": v(-92.2, 14.46) * mm});
            skLineSegment(sketch, "E7.2.0.10", {"start": v(-97, 15.43) * mm, "end": v(-97, 14.46) * mm});
            skLineSegment(sketch, "E7.2.0.11", {"start": v(-77.8, 15.43) * mm, "end": v(-77.8, 14.46) * mm});
            skLineSegment(sketch, "E7.2.0.12", {"start": v(-85, 14.46) * mm, "end": v(-84.7, 14.46) * mm});
            skLineSegment(sketch, "E7.2.0.13", {"start": v(-77.5, 15.43) * mm, "end": v(-77.5, 14.46) * mm});
            skLineSegment(sketch, "E7.2.0.14", {"start": v(-89.8, 15.43) * mm, "end": v(-89.8, 14.46) * mm});
            skLineSegment(sketch, "E7.2.0.15", {"start": v(-94.6, 15.43) * mm, "end": v(-94.6, 14.46) * mm});
            skLineSegment(sketch, "E7.2.0.16", {"start": v(-75.4, 15.43) * mm, "end": v(-75.4, 14.46) * mm});
            skLineSegment(sketch, "E7.2.0.17", {"start": v(-80.2, 15.43) * mm, "end": v(-80.2, 14.46) * mm});
            skLineSegment(sketch, "E7.2.0.18", {"start": v(-85, 15.43) * mm, "end": v(-85, 14.46) * mm});
            skLineSegment(sketch, "E7.2.0.19", {"start": v(-82.3, 15.43) * mm, "end": v(-82.3, 14.46) * mm});
            skLineSegment(sketch, "E7.2.0.20", {"start": v(-87.1, 15.43) * mm, "end": v(-87.1, 14.46) * mm});
            skLineSegment(sketch, "E7.2.0.21", {"start": v(-91.9, 15.43) * mm, "end": v(-91.9, 14.46) * mm});
            skLineSegment(sketch, "E7.2.0.22", {"start": v(-96.7, 15.43) * mm, "end": v(-96.7, 14.46) * mm});
            skLineSegment(sketch, "E7.2.0.23", {"start": v(-89.5, 15.43) * mm, "end": v(-89.5, 14.46) * mm});
            skLineSegment(sketch, "E7.2.0.24", {"start": v(-94.3, 15.43) * mm, "end": v(-94.3, 14.46) * mm});
            skLineSegment(sketch, "E7.2.0.25", {"start": v(-75.1, 15.43) * mm, "end": v(-75.1, 14.46) * mm});
            skLineSegment(sketch, "E7.2.0.26", {"start": v(-79.9, 15.43) * mm, "end": v(-79.9, 14.46) * mm});
            skLineSegment(sketch, "E7.2.0.27", {"start": v(-84.7, 15.43) * mm, "end": v(-84.7, 14.46) * mm});
            skLineSegment(sketch, "E7.2.0.28", {"start": v(-83.8, 14.46) * mm, "end": v(-83.5, 14.46) * mm});
            skLineSegment(sketch, "E7.2.0.29", {"start": v(-74.2, 14.46) * mm, "end": v(-73.9, 14.46) * mm});
            skLineSegment(sketch, "E7.2.0.30", {"start": v(-79, 14.46) * mm, "end": v(-78.7, 14.46) * mm});
            skLineSegment(sketch, "E7.2.0.31", {"start": v(-83.8, 15.43) * mm, "end": v(-83.8, 14.46) * mm});
            skLineSegment(sketch, "E7.2.0.32", {"start": v(-81.4, 14.46) * mm, "end": v(-81.1, 14.46) * mm});
            skLineSegment(sketch, "E7.2.0.33", {"start": v(-74.2, 15.43) * mm, "end": v(-74.2, 14.46) * mm});
            skLineSegment(sketch, "E7.2.0.34", {"start": v(-79, 15.43) * mm, "end": v(-79, 14.46) * mm});
            skLineSegment(sketch, "E7.2.0.35", {"start": v(-76.6, 14.46) * mm, "end": v(-76.3, 14.46) * mm});
            skLineSegment(sketch, "E7.2.0.36", {"start": v(-81.4, 15.43) * mm, "end": v(-81.4, 14.46) * mm});
            skLineSegment(sketch, "E7.2.0.37", {"start": v(-83.5, 15.43) * mm, "end": v(-83.5, 14.46) * mm});
            skLineSegment(sketch, "E7.2.0.38", {"start": v(-73.9, 15.43) * mm, "end": v(-73.9, 14.46) * mm});
            skLineSegment(sketch, "E7.2.0.39", {"start": v(-78.7, 15.43) * mm, "end": v(-78.7, 14.46) * mm});
            skLineSegment(sketch, "E7.2.0.40", {"start": v(-76.6, 15.43) * mm, "end": v(-76.6, 14.46) * mm});
            skLineSegment(sketch, "E7.2.0.41", {"start": v(-82.6, 15.43) * mm, "end": v(-82.3, 15.43) * mm});
            skLineSegment(sketch, "E7.2.0.42", {"start": v(-87.4, 15.43) * mm, "end": v(-87.1, 15.43) * mm});
            skLineSegment(sketch, "E7.2.0.43", {"start": v(-92.2, 15.43) * mm, "end": v(-91.9, 15.43) * mm});
            skLineSegment(sketch, "E7.2.0.44", {"start": v(-97, 15.43) * mm, "end": v(-96.7, 15.43) * mm});
            skLineSegment(sketch, "E7.2.0.45", {"start": v(-101.8, 14.46) * mm, "end": v(-100.6, 14.46) * mm, "construction": true});
            skLineSegment(sketch, "E7.2.0.46", {"start": v(-77.8, 15.43) * mm, "end": v(-77.5, 15.43) * mm});
            skLineSegment(sketch, "E7.2.0.47", {"start": v(-76.3, 15.43) * mm, "end": v(-76.3, 14.46) * mm});
            skLineSegment(sketch, "E7.2.0.48", {"start": v(-81.1, 15.43) * mm, "end": v(-81.1, 14.46) * mm});
            skLineSegment(sketch, "E7.2.0.49", {"start": v(-98.2, 14.46) * mm, "end": v(-97.9, 14.46) * mm});
            skLineSegment(sketch, "E7.2.0.50", {"start": v(-97, 14.46) * mm, "end": v(-96.7, 14.46) * mm});
            skLineSegment(sketch, "E7.2.0.51", {"start": v(-92.2, 14.46) * mm, "end": v(-91.9, 14.46) * mm});
            skLineSegment(sketch, "E7.2.0.52", {"start": v(-87.4, 14.46) * mm, "end": v(-87.1, 14.46) * mm});
            skLineSegment(sketch, "E7.2.0.53", {"start": v(-82.6, 14.46) * mm, "end": v(-82.3, 14.46) * mm});
            skLineSegment(sketch, "E7.2.0.54", {"start": v(-77.8, 14.46) * mm, "end": v(-77.5, 14.46) * mm});
            skLineSegment(sketch, "E7.2.0.55", {"start": v(-98.2, 15.43) * mm, "end": v(-98.2, 14.46) * mm});
            skLineSegment(sketch, "E7.2.0.56", {"start": v(-97.9, 15.43) * mm, "end": v(-97.9, 14.46) * mm});
            skLineSegment(sketch, "E7.2.0.57", {"start": v(-101.8, 15.43) * mm, "end": v(-101.5, 15.43) * mm});
            skLineSegment(sketch, "E7.2.0.58", {"start": v(-101.8, 14.46) * mm, "end": v(-101.5, 14.46) * mm});
            skLineSegment(sketch, "E7.2.0.59", {"start": v(-100.6, 15.43) * mm, "end": v(-100.3, 15.43) * mm});
            skLineSegment(sketch, "E7.2.0.60", {"start": v(-100.6, 14.46) * mm, "end": v(-100.3, 14.46) * mm});
            skLineSegment(sketch, "E7.2.0.61", {"start": v(-100.6, 15.43) * mm, "end": v(-100.6, 14.46) * mm});
            skLineSegment(sketch, "E7.2.0.62", {"start": v(-100.3, 15.43) * mm, "end": v(-100.3, 14.46) * mm});
            skLineSegment(sketch, "E7.2.0.63", {"start": v(-99.4, 15.43) * mm, "end": v(-99.1, 15.43) * mm});
            skLineSegment(sketch, "E7.2.0.64", {"start": v(-99.4, 14.46) * mm, "end": v(-99.1, 14.46) * mm});
            skLineSegment(sketch, "E7.2.0.65", {"start": v(-98.2, 15.43) * mm, "end": v(-97.9, 15.43) * mm});
            skLineSegment(sketch, "E7.2.0.66", {"start": v(-89.8, 15.43) * mm, "end": v(-89.5, 15.43) * mm});
            skLineSegment(sketch, "E7.2.0.67", {"start": v(-94.6, 15.43) * mm, "end": v(-94.3, 15.43) * mm});
            skLineSegment(sketch, "E7.2.0.68", {"start": v(-89.8, 14.46) * mm, "end": v(-89.5, 14.46) * mm});
            skLineSegment(sketch, "E7.2.0.69", {"start": v(-94.6, 14.46) * mm, "end": v(-94.3, 14.46) * mm});
            skLineSegment(sketch, "E7.2.0.70", {"start": v(-75.4, 14.46) * mm, "end": v(-75.1, 14.46) * mm});
            skLineSegment(sketch, "E7.2.0.71", {"start": v(-80.2, 14.46) * mm, "end": v(-79.9, 14.46) * mm});
            skLineSegment(sketch, "E7.2.0.72", {"start": v(-81.4, 15.43) * mm, "end": v(-81.1, 15.43) * mm});
            skLineSegment(sketch, "E7.2.0.73", {"start": v(-88.6, 14.46) * mm, "end": v(-88.3, 14.46) * mm});
            skLineSegment(sketch, "E7.2.0.74", {"start": v(-86.2, 15.43) * mm, "end": v(-85.9, 15.43) * mm});
            skLineSegment(sketch, "E7.2.0.75", {"start": v(-91, 15.43) * mm, "end": v(-90.7, 15.43) * mm});
            skLineSegment(sketch, "E7.2.0.76", {"start": v(-93.4, 14.46) * mm, "end": v(-93.1, 14.46) * mm});
            skLineSegment(sketch, "E7.2.0.77", {"start": v(-95.8, 15.43) * mm, "end": v(-95.5, 15.43) * mm});
            skLineSegment(sketch, "E7.2.0.78", {"start": v(-76.6, 15.43) * mm, "end": v(-76.3, 15.43) * mm});
            skLineSegment(sketch, "E7.2.0.79", {"start": v(-88.6, 15.43) * mm, "end": v(-88.3, 15.43) * mm});
            skLineSegment(sketch, "E7.2.0.80", {"start": v(-93.4, 15.43) * mm, "end": v(-93.1, 15.43) * mm});
            skLineSegment(sketch, "E7.2.0.81", {"start": v(-74.2, 15.43) * mm, "end": v(-73.9, 15.43) * mm});
            skLineSegment(sketch, "E7.2.0.82", {"start": v(-79, 15.43) * mm, "end": v(-78.7, 15.43) * mm});
            skLineSegment(sketch, "E7.2.0.83", {"start": v(-83.8, 15.43) * mm, "end": v(-83.5, 15.43) * mm});
            skLineSegment(sketch, "E7.2.0.84", {"start": v(-86.2, 14.46) * mm, "end": v(-85.9, 14.46) * mm});
            skLineSegment(sketch, "E7.2.0.85", {"start": v(-88.6, 15.43) * mm, "end": v(-88.6, 14.46) * mm});
            skLineSegment(sketch, "E7.2.0.86", {"start": v(-91, 14.46) * mm, "end": v(-90.7, 14.46) * mm});
            skLineSegment(sketch, "E7.2.0.87", {"start": v(-93.4, 15.43) * mm, "end": v(-93.4, 14.46) * mm});
            skLineSegment(sketch, "E7.2.0.88", {"start": v(-95.8, 14.46) * mm, "end": v(-95.5, 14.46) * mm});
            skLineSegment(sketch, "E7.2.0.89", {"start": v(-88.3, 15.43) * mm, "end": v(-88.3, 14.46) * mm});
            skLineSegment(sketch, "E7.2.0.90", {"start": v(-86.2, 15.43) * mm, "end": v(-86.2, 14.46) * mm});
            skLineSegment(sketch, "E7.2.0.91", {"start": v(-93.1, 15.43) * mm, "end": v(-93.1, 14.46) * mm});
            skLineSegment(sketch, "E7.2.0.92", {"start": v(-91, 15.43) * mm, "end": v(-91, 14.46) * mm});
            skLineSegment(sketch, "E7.2.0.93", {"start": v(-95.8, 15.43) * mm, "end": v(-95.8, 14.46) * mm});
            skLineSegment(sketch, "E7.2.0.94", {"start": v(-90.7, 15.43) * mm, "end": v(-90.7, 14.46) * mm});
            skLineSegment(sketch, "E7.2.0.95", {"start": v(-95.5, 15.43) * mm, "end": v(-95.5, 14.46) * mm});
            skLineSegment(sketch, "E7.2.0.96", {"start": v(-85.9, 15.43) * mm, "end": v(-85.9, 14.46) * mm});
            skLineSegment(sketch, "E7.3.0.0", {"start": v(-101.78, 13.59) * mm, "end": v(-101.78, 12.62) * mm});
            skLineSegment(sketch, "E7.3.0.1", {"start": v(-101.47, 13.59) * mm, "end": v(-101.47, 12.62) * mm});
            skLineSegment(sketch, "E7.3.0.2", {"start": v(-99.38, 13.59) * mm, "end": v(-99.38, 12.62) * mm});
            skLineSegment(sketch, "E7.3.0.3", {"start": v(-99.07, 13.59) * mm, "end": v(-99.07, 12.62) * mm});
            skLineSegment(sketch, "E7.3.0.4", {"start": v(-75.38, 13.59) * mm, "end": v(-75.07, 13.59) * mm});
            skLineSegment(sketch, "E7.3.0.5", {"start": v(-80.18, 13.59) * mm, "end": v(-79.87, 13.59) * mm});
            skLineSegment(sketch, "E7.3.0.6", {"start": v(-84.98, 13.59) * mm, "end": v(-84.67, 13.59) * mm});
            skLineSegment(sketch, "E7.3.0.7", {"start": v(-82.58, 13.59) * mm, "end": v(-82.58, 12.62) * mm});
            skLineSegment(sketch, "E7.3.0.8", {"start": v(-87.38, 13.59) * mm, "end": v(-87.38, 12.62) * mm});
            skLineSegment(sketch, "E7.3.0.9", {"start": v(-92.18, 13.59) * mm, "end": v(-92.18, 12.62) * mm});
            skLineSegment(sketch, "E7.3.0.10", {"start": v(-96.98, 13.59) * mm, "end": v(-96.98, 12.62) * mm});
            skLineSegment(sketch, "E7.3.0.11", {"start": v(-77.78, 13.59) * mm, "end": v(-77.78, 12.62) * mm});
            skLineSegment(sketch, "E7.3.0.12", {"start": v(-84.98, 12.62) * mm, "end": v(-84.67, 12.62) * mm});
            skLineSegment(sketch, "E7.3.0.13", {"start": v(-77.47, 13.59) * mm, "end": v(-77.47, 12.62) * mm});
            skLineSegment(sketch, "E7.3.0.14", {"start": v(-89.78, 13.59) * mm, "end": v(-89.78, 12.62) * mm});
            skLineSegment(sketch, "E7.3.0.15", {"start": v(-94.58, 13.59) * mm, "end": v(-94.58, 12.62) * mm});
            skLineSegment(sketch, "E7.3.0.16", {"start": v(-75.38, 13.59) * mm, "end": v(-75.38, 12.62) * mm});
            skLineSegment(sketch, "E7.3.0.17", {"start": v(-80.18, 13.59) * mm, "end": v(-80.18, 12.62) * mm});
            skLineSegment(sketch, "E7.3.0.18", {"start": v(-84.98, 13.59) * mm, "end": v(-84.98, 12.62) * mm});
            skLineSegment(sketch, "E7.3.0.19", {"start": v(-82.27, 13.59) * mm, "end": v(-82.27, 12.62) * mm});
            skLineSegment(sketch, "E7.3.0.20", {"start": v(-87.07, 13.59) * mm, "end": v(-87.07, 12.62) * mm});
            skLineSegment(sketch, "E7.3.0.21", {"start": v(-91.87, 13.59) * mm, "end": v(-91.87, 12.62) * mm});
            skLineSegment(sketch, "E7.3.0.22", {"start": v(-96.67, 13.59) * mm, "end": v(-96.67, 12.62) * mm});
            skLineSegment(sketch, "E7.3.0.23", {"start": v(-89.47, 13.59) * mm, "end": v(-89.47, 12.62) * mm});
            skLineSegment(sketch, "E7.3.0.24", {"start": v(-94.27, 13.59) * mm, "end": v(-94.27, 12.62) * mm});
            skLineSegment(sketch, "E7.3.0.25", {"start": v(-75.07, 13.59) * mm, "end": v(-75.07, 12.62) * mm});
            skLineSegment(sketch, "E7.3.0.26", {"start": v(-79.87, 13.59) * mm, "end": v(-79.87, 12.62) * mm});
            skLineSegment(sketch, "E7.3.0.27", {"start": v(-84.67, 13.59) * mm, "end": v(-84.67, 12.62) * mm});
            skLineSegment(sketch, "E7.3.0.28", {"start": v(-83.78, 12.62) * mm, "end": v(-83.47, 12.62) * mm});
            skLineSegment(sketch, "E7.3.0.29", {"start": v(-74.18, 12.62) * mm, "end": v(-73.87, 12.62) * mm});
            skLineSegment(sketch, "E7.3.0.30", {"start": v(-78.98, 12.62) * mm, "end": v(-78.67, 12.62) * mm});
            skLineSegment(sketch, "E7.3.0.31", {"start": v(-83.78, 13.59) * mm, "end": v(-83.78, 12.62) * mm});
            skLineSegment(sketch, "E7.3.0.32", {"start": v(-81.38, 12.62) * mm, "end": v(-81.07, 12.62) * mm});
            skLineSegment(sketch, "E7.3.0.33", {"start": v(-74.18, 13.59) * mm, "end": v(-74.18, 12.62) * mm});
            skLineSegment(sketch, "E7.3.0.34", {"start": v(-78.98, 13.59) * mm, "end": v(-78.98, 12.62) * mm});
            skLineSegment(sketch, "E7.3.0.35", {"start": v(-76.58, 12.62) * mm, "end": v(-76.27, 12.62) * mm});
            skLineSegment(sketch, "E7.3.0.36", {"start": v(-81.38, 13.59) * mm, "end": v(-81.38, 12.62) * mm});
            skLineSegment(sketch, "E7.3.0.37", {"start": v(-83.47, 13.59) * mm, "end": v(-83.47, 12.62) * mm});
            skLineSegment(sketch, "E7.3.0.38", {"start": v(-73.87, 13.59) * mm, "end": v(-73.87, 12.62) * mm});
            skLineSegment(sketch, "E7.3.0.39", {"start": v(-78.67, 13.59) * mm, "end": v(-78.67, 12.62) * mm});
            skLineSegment(sketch, "E7.3.0.40", {"start": v(-76.58, 13.59) * mm, "end": v(-76.58, 12.62) * mm});
            skLineSegment(sketch, "E7.3.0.41", {"start": v(-82.58, 13.59) * mm, "end": v(-82.27, 13.59) * mm});
            skLineSegment(sketch, "E7.3.0.42", {"start": v(-87.38, 13.59) * mm, "end": v(-87.07, 13.59) * mm});
            skLineSegment(sketch, "E7.3.0.43", {"start": v(-92.18, 13.59) * mm, "end": v(-91.87, 13.59) * mm});
            skLineSegment(sketch, "E7.3.0.44", {"start": v(-96.98, 13.59) * mm, "end": v(-96.67, 13.59) * mm});
            skLineSegment(sketch, "E7.3.0.45", {"start": v(-101.78, 12.62) * mm, "end": v(-100.58, 12.62) * mm, "construction": true});
            skLineSegment(sketch, "E7.3.0.46", {"start": v(-77.78, 13.59) * mm, "end": v(-77.47, 13.59) * mm});
            skLineSegment(sketch, "E7.3.0.47", {"start": v(-76.27, 13.59) * mm, "end": v(-76.27, 12.62) * mm});
            skLineSegment(sketch, "E7.3.0.48", {"start": v(-81.07, 13.59) * mm, "end": v(-81.07, 12.62) * mm});
            skLineSegment(sketch, "E7.3.0.49", {"start": v(-98.18, 12.62) * mm, "end": v(-97.87, 12.62) * mm});
            skLineSegment(sketch, "E7.3.0.50", {"start": v(-96.98, 12.62) * mm, "end": v(-96.67, 12.62) * mm});
            skLineSegment(sketch, "E7.3.0.51", {"start": v(-92.18, 12.62) * mm, "end": v(-91.87, 12.62) * mm});
            skLineSegment(sketch, "E7.3.0.52", {"start": v(-87.38, 12.62) * mm, "end": v(-87.07, 12.62) * mm});
            skLineSegment(sketch, "E7.3.0.53", {"start": v(-82.58, 12.62) * mm, "end": v(-82.27, 12.62) * mm});
            skLineSegment(sketch, "E7.3.0.54", {"start": v(-77.78, 12.62) * mm, "end": v(-77.47, 12.62) * mm});
            skLineSegment(sketch, "E7.3.0.55", {"start": v(-98.18, 13.59) * mm, "end": v(-98.18, 12.62) * mm});
            skLineSegment(sketch, "E7.3.0.56", {"start": v(-97.87, 13.59) * mm, "end": v(-97.87, 12.62) * mm});
            skLineSegment(sketch, "E7.3.0.57", {"start": v(-101.78, 13.59) * mm, "end": v(-101.47, 13.59) * mm});
            skLineSegment(sketch, "E7.3.0.58", {"start": v(-101.78, 12.62) * mm, "end": v(-101.47, 12.62) * mm});
            skLineSegment(sketch, "E7.3.0.59", {"start": v(-100.58, 13.59) * mm, "end": v(-100.27, 13.59) * mm});
            skLineSegment(sketch, "E7.3.0.60", {"start": v(-100.58, 12.62) * mm, "end": v(-100.27, 12.62) * mm});
            skLineSegment(sketch, "E7.3.0.61", {"start": v(-100.58, 13.59) * mm, "end": v(-100.58, 12.62) * mm});
            skLineSegment(sketch, "E7.3.0.62", {"start": v(-100.27, 13.59) * mm, "end": v(-100.27, 12.62) * mm});
            skLineSegment(sketch, "E7.3.0.63", {"start": v(-99.38, 13.59) * mm, "end": v(-99.07, 13.59) * mm});
            skLineSegment(sketch, "E7.3.0.64", {"start": v(-99.38, 12.62) * mm, "end": v(-99.07, 12.62) * mm});
            skLineSegment(sketch, "E7.3.0.65", {"start": v(-98.18, 13.59) * mm, "end": v(-97.87, 13.59) * mm});
            skLineSegment(sketch, "E7.3.0.66", {"start": v(-89.78, 13.59) * mm, "end": v(-89.47, 13.59) * mm});
            skLineSegment(sketch, "E7.3.0.67", {"start": v(-94.58, 13.59) * mm, "end": v(-94.27, 13.59) * mm});
            skLineSegment(sketch, "E7.3.0.68", {"start": v(-89.78, 12.62) * mm, "end": v(-89.47, 12.62) * mm});
            skLineSegment(sketch, "E7.3.0.69", {"start": v(-94.58, 12.62) * mm, "end": v(-94.27, 12.62) * mm});
            skLineSegment(sketch, "E7.3.0.70", {"start": v(-75.38, 12.62) * mm, "end": v(-75.07, 12.62) * mm});
            skLineSegment(sketch, "E7.3.0.71", {"start": v(-80.18, 12.62) * mm, "end": v(-79.87, 12.62) * mm});
            skLineSegment(sketch, "E7.3.0.72", {"start": v(-81.38, 13.59) * mm, "end": v(-81.07, 13.59) * mm});
            skLineSegment(sketch, "E7.3.0.73", {"start": v(-88.58, 12.62) * mm, "end": v(-88.27, 12.62) * mm});
            skLineSegment(sketch, "E7.3.0.74", {"start": v(-86.18, 13.59) * mm, "end": v(-85.87, 13.59) * mm});
            skLineSegment(sketch, "E7.3.0.75", {"start": v(-90.98, 13.59) * mm, "end": v(-90.67, 13.59) * mm});
            skLineSegment(sketch, "E7.3.0.76", {"start": v(-93.38, 12.62) * mm, "end": v(-93.07, 12.62) * mm});
            skLineSegment(sketch, "E7.3.0.77", {"start": v(-95.78, 13.59) * mm, "end": v(-95.47, 13.59) * mm});
            skLineSegment(sketch, "E7.3.0.78", {"start": v(-76.58, 13.59) * mm, "end": v(-76.27, 13.59) * mm});
            skLineSegment(sketch, "E7.3.0.79", {"start": v(-88.58, 13.59) * mm, "end": v(-88.27, 13.59) * mm});
            skLineSegment(sketch, "E7.3.0.80", {"start": v(-93.38, 13.59) * mm, "end": v(-93.07, 13.59) * mm});
            skLineSegment(sketch, "E7.3.0.81", {"start": v(-74.18, 13.59) * mm, "end": v(-73.87, 13.59) * mm});
            skLineSegment(sketch, "E7.3.0.82", {"start": v(-78.98, 13.59) * mm, "end": v(-78.67, 13.59) * mm});
            skLineSegment(sketch, "E7.3.0.83", {"start": v(-83.78, 13.59) * mm, "end": v(-83.47, 13.59) * mm});
            skLineSegment(sketch, "E7.3.0.84", {"start": v(-86.18, 12.62) * mm, "end": v(-85.87, 12.62) * mm});
            skLineSegment(sketch, "E7.3.0.85", {"start": v(-88.58, 13.59) * mm, "end": v(-88.58, 12.62) * mm});
            skLineSegment(sketch, "E7.3.0.86", {"start": v(-90.98, 12.62) * mm, "end": v(-90.67, 12.62) * mm});
            skLineSegment(sketch, "E7.3.0.87", {"start": v(-93.38, 13.59) * mm, "end": v(-93.38, 12.62) * mm});
            skLineSegment(sketch, "E7.3.0.88", {"start": v(-95.78, 12.62) * mm, "end": v(-95.47, 12.62) * mm});
            skLineSegment(sketch, "E7.3.0.89", {"start": v(-88.27, 13.59) * mm, "end": v(-88.27, 12.62) * mm});
            skLineSegment(sketch, "E7.3.0.90", {"start": v(-86.18, 13.59) * mm, "end": v(-86.18, 12.62) * mm});
            skLineSegment(sketch, "E7.3.0.91", {"start": v(-93.07, 13.59) * mm, "end": v(-93.07, 12.62) * mm});
            skLineSegment(sketch, "E7.3.0.92", {"start": v(-90.98, 13.59) * mm, "end": v(-90.98, 12.62) * mm});
            skLineSegment(sketch, "E7.3.0.93", {"start": v(-95.78, 13.59) * mm, "end": v(-95.78, 12.62) * mm});
            skLineSegment(sketch, "E7.3.0.94", {"start": v(-90.67, 13.59) * mm, "end": v(-90.67, 12.62) * mm});
            skLineSegment(sketch, "E7.3.0.95", {"start": v(-95.47, 13.59) * mm, "end": v(-95.47, 12.62) * mm});
            skLineSegment(sketch, "E7.3.0.96", {"start": v(-85.87, 13.59) * mm, "end": v(-85.87, 12.62) * mm});
            skLineSegment(sketch, "E7.4.0.0", {"start": v(-101.77, 11.74) * mm, "end": v(-101.77, 10.77) * mm});
            skLineSegment(sketch, "E7.4.0.1", {"start": v(-101.46, 11.74) * mm, "end": v(-101.46, 10.77) * mm});
            skLineSegment(sketch, "E7.4.0.2", {"start": v(-99.37, 11.74) * mm, "end": v(-99.37, 10.77) * mm});
            skLineSegment(sketch, "E7.4.0.3", {"start": v(-99.06, 11.74) * mm, "end": v(-99.06, 10.77) * mm});
            skLineSegment(sketch, "E7.4.0.4", {"start": v(-75.37, 11.74) * mm, "end": v(-75.06, 11.74) * mm});
            skLineSegment(sketch, "E7.4.0.5", {"start": v(-80.17, 11.74) * mm, "end": v(-79.86, 11.74) * mm});
            skLineSegment(sketch, "E7.4.0.6", {"start": v(-84.97, 11.74) * mm, "end": v(-84.66, 11.74) * mm});
            skLineSegment(sketch, "E7.4.0.7", {"start": v(-82.57, 11.74) * mm, "end": v(-82.57, 10.77) * mm});
            skLineSegment(sketch, "E7.4.0.8", {"start": v(-87.37, 11.74) * mm, "end": v(-87.37, 10.77) * mm});
            skLineSegment(sketch, "E7.4.0.9", {"start": v(-92.17, 11.74) * mm, "end": v(-92.17, 10.77) * mm});
            skLineSegment(sketch, "E7.4.0.10", {"start": v(-96.97, 11.74) * mm, "end": v(-96.97, 10.77) * mm});
            skLineSegment(sketch, "E7.4.0.11", {"start": v(-77.77, 11.74) * mm, "end": v(-77.77, 10.77) * mm});
            skLineSegment(sketch, "E7.4.0.12", {"start": v(-84.97, 10.77) * mm, "end": v(-84.66, 10.77) * mm});
            skLineSegment(sketch, "E7.4.0.13", {"start": v(-77.46, 11.74) * mm, "end": v(-77.46, 10.77) * mm});
            skLineSegment(sketch, "E7.4.0.14", {"start": v(-89.77, 11.74) * mm, "end": v(-89.77, 10.77) * mm});
            skLineSegment(sketch, "E7.4.0.15", {"start": v(-94.57, 11.74) * mm, "end": v(-94.57, 10.77) * mm});
            skLineSegment(sketch, "E7.4.0.16", {"start": v(-75.37, 11.74) * mm, "end": v(-75.37, 10.77) * mm});
            skLineSegment(sketch, "E7.4.0.17", {"start": v(-80.17, 11.74) * mm, "end": v(-80.17, 10.77) * mm});
            skLineSegment(sketch, "E7.4.0.18", {"start": v(-84.97, 11.74) * mm, "end": v(-84.97, 10.77) * mm});
            skLineSegment(sketch, "E7.4.0.19", {"start": v(-82.26, 11.74) * mm, "end": v(-82.26, 10.77) * mm});
            skLineSegment(sketch, "E7.4.0.20", {"start": v(-87.06, 11.74) * mm, "end": v(-87.06, 10.77) * mm});
            skLineSegment(sketch, "E7.4.0.21", {"start": v(-91.86, 11.74) * mm, "end": v(-91.86, 10.77) * mm});
            skLineSegment(sketch, "E7.4.0.22", {"start": v(-96.66, 11.74) * mm, "end": v(-96.66, 10.77) * mm});
            skLineSegment(sketch, "E7.4.0.23", {"start": v(-89.46, 11.74) * mm, "end": v(-89.46, 10.77) * mm});
            skLineSegment(sketch, "E7.4.0.24", {"start": v(-94.26, 11.74) * mm, "end": v(-94.26, 10.77) * mm});
            skLineSegment(sketch, "E7.4.0.25", {"start": v(-75.06, 11.74) * mm, "end": v(-75.06, 10.77) * mm});
            skLineSegment(sketch, "E7.4.0.26", {"start": v(-79.86, 11.74) * mm, "end": v(-79.86, 10.77) * mm});
            skLineSegment(sketch, "E7.4.0.27", {"start": v(-84.66, 11.74) * mm, "end": v(-84.66, 10.77) * mm});
            skLineSegment(sketch, "E7.4.0.28", {"start": v(-83.77, 10.77) * mm, "end": v(-83.46, 10.77) * mm});
            skLineSegment(sketch, "E7.4.0.29", {"start": v(-74.17, 10.77) * mm, "end": v(-73.86, 10.77) * mm});
            skLineSegment(sketch, "E7.4.0.30", {"start": v(-78.97, 10.77) * mm, "end": v(-78.66, 10.77) * mm});
            skLineSegment(sketch, "E7.4.0.31", {"start": v(-83.77, 11.74) * mm, "end": v(-83.77, 10.77) * mm});
            skLineSegment(sketch, "E7.4.0.32", {"start": v(-81.37, 10.77) * mm, "end": v(-81.06, 10.77) * mm});
            skLineSegment(sketch, "E7.4.0.33", {"start": v(-74.17, 11.74) * mm, "end": v(-74.17, 10.77) * mm});
            skLineSegment(sketch, "E7.4.0.34", {"start": v(-78.97, 11.74) * mm, "end": v(-78.97, 10.77) * mm});
            skLineSegment(sketch, "E7.4.0.35", {"start": v(-76.57, 10.77) * mm, "end": v(-76.26, 10.77) * mm});
            skLineSegment(sketch, "E7.4.0.36", {"start": v(-81.37, 11.74) * mm, "end": v(-81.37, 10.77) * mm});
            skLineSegment(sketch, "E7.4.0.37", {"start": v(-83.46, 11.74) * mm, "end": v(-83.46, 10.77) * mm});
            skLineSegment(sketch, "E7.4.0.38", {"start": v(-73.86, 11.74) * mm, "end": v(-73.86, 10.77) * mm});
            skLineSegment(sketch, "E7.4.0.39", {"start": v(-78.66, 11.74) * mm, "end": v(-78.66, 10.77) * mm});
            skLineSegment(sketch, "E7.4.0.40", {"start": v(-76.57, 11.74) * mm, "end": v(-76.57, 10.77) * mm});
            skLineSegment(sketch, "E7.4.0.41", {"start": v(-82.57, 11.74) * mm, "end": v(-82.26, 11.74) * mm});
            skLineSegment(sketch, "E7.4.0.42", {"start": v(-87.37, 11.74) * mm, "end": v(-87.06, 11.74) * mm});
            skLineSegment(sketch, "E7.4.0.43", {"start": v(-92.17, 11.74) * mm, "end": v(-91.86, 11.74) * mm});
            skLineSegment(sketch, "E7.4.0.44", {"start": v(-96.97, 11.74) * mm, "end": v(-96.66, 11.74) * mm});
            skLineSegment(sketch, "E7.4.0.45", {"start": v(-101.77, 10.77) * mm, "end": v(-100.57, 10.77) * mm, "construction": true});
            skLineSegment(sketch, "E7.4.0.46", {"start": v(-77.77, 11.74) * mm, "end": v(-77.46, 11.74) * mm});
            skLineSegment(sketch, "E7.4.0.47", {"start": v(-76.26, 11.74) * mm, "end": v(-76.26, 10.77) * mm});
            skLineSegment(sketch, "E7.4.0.48", {"start": v(-81.06, 11.74) * mm, "end": v(-81.06, 10.77) * mm});
            skLineSegment(sketch, "E7.4.0.49", {"start": v(-98.17, 10.77) * mm, "end": v(-97.86, 10.77) * mm});
            skLineSegment(sketch, "E7.4.0.50", {"start": v(-96.97, 10.77) * mm, "end": v(-96.66, 10.77) * mm});
            skLineSegment(sketch, "E7.4.0.51", {"start": v(-92.17, 10.77) * mm, "end": v(-91.86, 10.77) * mm});
            skLineSegment(sketch, "E7.4.0.52", {"start": v(-87.37, 10.77) * mm, "end": v(-87.06, 10.77) * mm});
            skLineSegment(sketch, "E7.4.0.53", {"start": v(-82.57, 10.77) * mm, "end": v(-82.26, 10.77) * mm});
            skLineSegment(sketch, "E7.4.0.54", {"start": v(-77.77, 10.77) * mm, "end": v(-77.46, 10.77) * mm});
            skLineSegment(sketch, "E7.4.0.55", {"start": v(-98.17, 11.74) * mm, "end": v(-98.17, 10.77) * mm});
            skLineSegment(sketch, "E7.4.0.56", {"start": v(-97.86, 11.74) * mm, "end": v(-97.86, 10.77) * mm});
            skLineSegment(sketch, "E7.4.0.57", {"start": v(-101.77, 11.74) * mm, "end": v(-101.46, 11.74) * mm});
            skLineSegment(sketch, "E7.4.0.58", {"start": v(-101.77, 10.77) * mm, "end": v(-101.46, 10.77) * mm});
            skLineSegment(sketch, "E7.4.0.59", {"start": v(-100.57, 11.74) * mm, "end": v(-100.26, 11.74) * mm});
            skLineSegment(sketch, "E7.4.0.60", {"start": v(-100.57, 10.77) * mm, "end": v(-100.26, 10.77) * mm});
            skLineSegment(sketch, "E7.4.0.61", {"start": v(-100.57, 11.74) * mm, "end": v(-100.57, 10.77) * mm});
            skLineSegment(sketch, "E7.4.0.62", {"start": v(-100.26, 11.74) * mm, "end": v(-100.26, 10.77) * mm});
            skLineSegment(sketch, "E7.4.0.63", {"start": v(-99.37, 11.74) * mm, "end": v(-99.06, 11.74) * mm});
            skLineSegment(sketch, "E7.4.0.64", {"start": v(-99.37, 10.77) * mm, "end": v(-99.06, 10.77) * mm});
            skLineSegment(sketch, "E7.4.0.65", {"start": v(-98.17, 11.74) * mm, "end": v(-97.86, 11.74) * mm});
            skLineSegment(sketch, "E7.4.0.66", {"start": v(-89.77, 11.74) * mm, "end": v(-89.46, 11.74) * mm});
            skLineSegment(sketch, "E7.4.0.67", {"start": v(-94.57, 11.74) * mm, "end": v(-94.26, 11.74) * mm});
            skLineSegment(sketch, "E7.4.0.68", {"start": v(-89.77, 10.77) * mm, "end": v(-89.46, 10.77) * mm});
            skLineSegment(sketch, "E7.4.0.69", {"start": v(-94.57, 10.77) * mm, "end": v(-94.26, 10.77) * mm});
            skLineSegment(sketch, "E7.4.0.70", {"start": v(-75.37, 10.77) * mm, "end": v(-75.06, 10.77) * mm});
            skLineSegment(sketch, "E7.4.0.71", {"start": v(-80.17, 10.77) * mm, "end": v(-79.86, 10.77) * mm});
            skLineSegment(sketch, "E7.4.0.72", {"start": v(-81.37, 11.74) * mm, "end": v(-81.06, 11.74) * mm});
            skLineSegment(sketch, "E7.4.0.73", {"start": v(-88.57, 10.77) * mm, "end": v(-88.26, 10.77) * mm});
            skLineSegment(sketch, "E7.4.0.74", {"start": v(-86.17, 11.74) * mm, "end": v(-85.86, 11.74) * mm});
            skLineSegment(sketch, "E7.4.0.75", {"start": v(-90.97, 11.74) * mm, "end": v(-90.66, 11.74) * mm});
            skLineSegment(sketch, "E7.4.0.76", {"start": v(-93.37, 10.77) * mm, "end": v(-93.06, 10.77) * mm});
            skLineSegment(sketch, "E7.4.0.77", {"start": v(-95.77, 11.74) * mm, "end": v(-95.46, 11.74) * mm});
            skLineSegment(sketch, "E7.4.0.78", {"start": v(-76.57, 11.74) * mm, "end": v(-76.26, 11.74) * mm});
            skLineSegment(sketch, "E7.4.0.79", {"start": v(-88.57, 11.74) * mm, "end": v(-88.26, 11.74) * mm});
            skLineSegment(sketch, "E7.4.0.80", {"start": v(-93.37, 11.74) * mm, "end": v(-93.06, 11.74) * mm});
            skLineSegment(sketch, "E7.4.0.81", {"start": v(-74.17, 11.74) * mm, "end": v(-73.86, 11.74) * mm});
            skLineSegment(sketch, "E7.4.0.82", {"start": v(-78.97, 11.74) * mm, "end": v(-78.66, 11.74) * mm});
            skLineSegment(sketch, "E7.4.0.83", {"start": v(-83.77, 11.74) * mm, "end": v(-83.46, 11.74) * mm});
            skLineSegment(sketch, "E7.4.0.84", {"start": v(-86.17, 10.77) * mm, "end": v(-85.86, 10.77) * mm});
            skLineSegment(sketch, "E7.4.0.85", {"start": v(-88.57, 11.74) * mm, "end": v(-88.57, 10.77) * mm});
            skLineSegment(sketch, "E7.4.0.86", {"start": v(-90.97, 10.77) * mm, "end": v(-90.66, 10.77) * mm});
            skLineSegment(sketch, "E7.4.0.87", {"start": v(-93.37, 11.74) * mm, "end": v(-93.37, 10.77) * mm});
            skLineSegment(sketch, "E7.4.0.88", {"start": v(-95.77, 10.77) * mm, "end": v(-95.46, 10.77) * mm});
            skLineSegment(sketch, "E7.4.0.89", {"start": v(-88.26, 11.74) * mm, "end": v(-88.26, 10.77) * mm});
            skLineSegment(sketch, "E7.4.0.90", {"start": v(-86.17, 11.74) * mm, "end": v(-86.17, 10.77) * mm});
            skLineSegment(sketch, "E7.4.0.91", {"start": v(-93.06, 11.74) * mm, "end": v(-93.06, 10.77) * mm});
            skLineSegment(sketch, "E7.4.0.92", {"start": v(-90.97, 11.74) * mm, "end": v(-90.97, 10.77) * mm});
            skLineSegment(sketch, "E7.4.0.93", {"start": v(-95.77, 11.74) * mm, "end": v(-95.77, 10.77) * mm});
            skLineSegment(sketch, "E7.4.0.94", {"start": v(-90.66, 11.74) * mm, "end": v(-90.66, 10.77) * mm});
            skLineSegment(sketch, "E7.4.0.95", {"start": v(-95.46, 11.74) * mm, "end": v(-95.46, 10.77) * mm});
            skLineSegment(sketch, "E7.4.0.96", {"start": v(-85.86, 11.74) * mm, "end": v(-85.86, 10.77) * mm});
            skLineSegment(sketch, "E7.5.0.0", {"start": v(-101.75, 9.9) * mm, "end": v(-101.75, 8.93) * mm});
            skLineSegment(sketch, "E7.5.0.1", {"start": v(-101.44, 9.9) * mm, "end": v(-101.44, 8.93) * mm});
            skLineSegment(sketch, "E7.5.0.2", {"start": v(-99.35, 9.9) * mm, "end": v(-99.35, 8.93) * mm});
            skLineSegment(sketch, "E7.5.0.3", {"start": v(-99.04, 9.9) * mm, "end": v(-99.04, 8.93) * mm});
            skLineSegment(sketch, "E7.5.0.4", {"start": v(-75.35, 9.9) * mm, "end": v(-75.04, 9.9) * mm});
            skLineSegment(sketch, "E7.5.0.5", {"start": v(-80.15, 9.9) * mm, "end": v(-79.84, 9.9) * mm});
            skLineSegment(sketch, "E7.5.0.6", {"start": v(-84.95, 9.9) * mm, "end": v(-84.64, 9.9) * mm});
            skLineSegment(sketch, "E7.5.0.7", {"start": v(-82.55, 9.9) * mm, "end": v(-82.55, 8.93) * mm});
            skLineSegment(sketch, "E7.5.0.8", {"start": v(-87.35, 9.9) * mm, "end": v(-87.35, 8.93) * mm});
            skLineSegment(sketch, "E7.5.0.9", {"start": v(-92.15, 9.9) * mm, "end": v(-92.15, 8.93) * mm});
            skLineSegment(sketch, "E7.5.0.10", {"start": v(-96.95, 9.9) * mm, "end": v(-96.95, 8.93) * mm});
            skLineSegment(sketch, "E7.5.0.11", {"start": v(-77.75, 9.9) * mm, "end": v(-77.75, 8.93) * mm});
            skLineSegment(sketch, "E7.5.0.12", {"start": v(-84.95, 8.93) * mm, "end": v(-84.64, 8.93) * mm});
            skLineSegment(sketch, "E7.5.0.13", {"start": v(-77.44, 9.9) * mm, "end": v(-77.44, 8.93) * mm});
            skLineSegment(sketch, "E7.5.0.14", {"start": v(-89.75, 9.9) * mm, "end": v(-89.75, 8.93) * mm});
            skLineSegment(sketch, "E7.5.0.15", {"start": v(-94.55, 9.9) * mm, "end": v(-94.55, 8.93) * mm});
            skLineSegment(sketch, "E7.5.0.16", {"start": v(-75.35, 9.9) * mm, "end": v(-75.35, 8.93) * mm});
            skLineSegment(sketch, "E7.5.0.17", {"start": v(-80.15, 9.9) * mm, "end": v(-80.15, 8.93) * mm});
            skLineSegment(sketch, "E7.5.0.18", {"start": v(-84.95, 9.9) * mm, "end": v(-84.95, 8.93) * mm});
            skLineSegment(sketch, "E7.5.0.19", {"start": v(-82.24, 9.9) * mm, "end": v(-82.24, 8.93) * mm});
            skLineSegment(sketch, "E7.5.0.20", {"start": v(-87.04, 9.9) * mm, "end": v(-87.04, 8.93) * mm});
            skLineSegment(sketch, "E7.5.0.21", {"start": v(-91.84, 9.9) * mm, "end": v(-91.84, 8.93) * mm});
            skLineSegment(sketch, "E7.5.0.22", {"start": v(-96.64, 9.9) * mm, "end": v(-96.64, 8.93) * mm});
            skLineSegment(sketch, "E7.5.0.23", {"start": v(-89.44, 9.9) * mm, "end": v(-89.44, 8.93) * mm});
            skLineSegment(sketch, "E7.5.0.24", {"start": v(-94.24, 9.9) * mm, "end": v(-94.24, 8.93) * mm});
            skLineSegment(sketch, "E7.5.0.25", {"start": v(-75.04, 9.9) * mm, "end": v(-75.04, 8.93) * mm});
            skLineSegment(sketch, "E7.5.0.26", {"start": v(-79.84, 9.9) * mm, "end": v(-79.84, 8.93) * mm});
            skLineSegment(sketch, "E7.5.0.27", {"start": v(-84.64, 9.9) * mm, "end": v(-84.64, 8.93) * mm});
            skLineSegment(sketch, "E7.5.0.28", {"start": v(-83.75, 8.93) * mm, "end": v(-83.44, 8.93) * mm});
            skLineSegment(sketch, "E7.5.0.29", {"start": v(-74.15, 8.93) * mm, "end": v(-73.84, 8.93) * mm});
            skLineSegment(sketch, "E7.5.0.30", {"start": v(-78.95, 8.93) * mm, "end": v(-78.64, 8.93) * mm});
            skLineSegment(sketch, "E7.5.0.31", {"start": v(-83.75, 9.9) * mm, "end": v(-83.75, 8.93) * mm});
            skLineSegment(sketch, "E7.5.0.32", {"start": v(-81.35, 8.93) * mm, "end": v(-81.04, 8.93) * mm});
            skLineSegment(sketch, "E7.5.0.33", {"start": v(-74.15, 9.9) * mm, "end": v(-74.15, 8.93) * mm});
            skLineSegment(sketch, "E7.5.0.34", {"start": v(-78.95, 9.9) * mm, "end": v(-78.95, 8.93) * mm});
            skLineSegment(sketch, "E7.5.0.35", {"start": v(-76.55, 8.93) * mm, "end": v(-76.24, 8.93) * mm});
            skLineSegment(sketch, "E7.5.0.36", {"start": v(-81.35, 9.9) * mm, "end": v(-81.35, 8.93) * mm});
            skLineSegment(sketch, "E7.5.0.37", {"start": v(-83.44, 9.9) * mm, "end": v(-83.44, 8.93) * mm});
            skLineSegment(sketch, "E7.5.0.38", {"start": v(-73.84, 9.9) * mm, "end": v(-73.84, 8.93) * mm});
            skLineSegment(sketch, "E7.5.0.39", {"start": v(-78.64, 9.9) * mm, "end": v(-78.64, 8.93) * mm});
            skLineSegment(sketch, "E7.5.0.40", {"start": v(-76.55, 9.9) * mm, "end": v(-76.55, 8.93) * mm});
            skLineSegment(sketch, "E7.5.0.41", {"start": v(-82.55, 9.9) * mm, "end": v(-82.24, 9.9) * mm});
            skLineSegment(sketch, "E7.5.0.42", {"start": v(-87.35, 9.9) * mm, "end": v(-87.04, 9.9) * mm});
            skLineSegment(sketch, "E7.5.0.43", {"start": v(-92.15, 9.9) * mm, "end": v(-91.84, 9.9) * mm});
            skLineSegment(sketch, "E7.5.0.44", {"start": v(-96.95, 9.9) * mm, "end": v(-96.64, 9.9) * mm});
            skLineSegment(sketch, "E7.5.0.45", {"start": v(-101.75, 8.93) * mm, "end": v(-100.55, 8.93) * mm, "construction": true});
            skLineSegment(sketch, "E7.5.0.46", {"start": v(-77.75, 9.9) * mm, "end": v(-77.44, 9.9) * mm});
            skLineSegment(sketch, "E7.5.0.47", {"start": v(-76.24, 9.9) * mm, "end": v(-76.24, 8.93) * mm});
            skLineSegment(sketch, "E7.5.0.48", {"start": v(-81.04, 9.9) * mm, "end": v(-81.04, 8.93) * mm});
            skLineSegment(sketch, "E7.5.0.49", {"start": v(-98.15, 8.93) * mm, "end": v(-97.84, 8.93) * mm});
            skLineSegment(sketch, "E7.5.0.50", {"start": v(-96.95, 8.93) * mm, "end": v(-96.64, 8.93) * mm});
            skLineSegment(sketch, "E7.5.0.51", {"start": v(-92.15, 8.93) * mm, "end": v(-91.84, 8.93) * mm});
            skLineSegment(sketch, "E7.5.0.52", {"start": v(-87.35, 8.93) * mm, "end": v(-87.04, 8.93) * mm});
            skLineSegment(sketch, "E7.5.0.53", {"start": v(-82.55, 8.93) * mm, "end": v(-82.24, 8.93) * mm});
            skLineSegment(sketch, "E7.5.0.54", {"start": v(-77.75, 8.93) * mm, "end": v(-77.44, 8.93) * mm});
            skLineSegment(sketch, "E7.5.0.55", {"start": v(-98.15, 9.9) * mm, "end": v(-98.15, 8.93) * mm});
            skLineSegment(sketch, "E7.5.0.56", {"start": v(-97.84, 9.9) * mm, "end": v(-97.84, 8.93) * mm});
            skLineSegment(sketch, "E7.5.0.57", {"start": v(-101.75, 9.9) * mm, "end": v(-101.44, 9.9) * mm});
            skLineSegment(sketch, "E7.5.0.58", {"start": v(-101.75, 8.93) * mm, "end": v(-101.44, 8.93) * mm});
            skLineSegment(sketch, "E7.5.0.59", {"start": v(-100.55, 9.9) * mm, "end": v(-100.24, 9.9) * mm});
            skLineSegment(sketch, "E7.5.0.60", {"start": v(-100.55, 8.93) * mm, "end": v(-100.24, 8.93) * mm});
            skLineSegment(sketch, "E7.5.0.61", {"start": v(-100.55, 9.9) * mm, "end": v(-100.55, 8.93) * mm});
            skLineSegment(sketch, "E7.5.0.62", {"start": v(-100.24, 9.9) * mm, "end": v(-100.24, 8.93) * mm});
            skLineSegment(sketch, "E7.5.0.63", {"start": v(-99.35, 9.9) * mm, "end": v(-99.04, 9.9) * mm});
            skLineSegment(sketch, "E7.5.0.64", {"start": v(-99.35, 8.93) * mm, "end": v(-99.04, 8.93) * mm});
            skLineSegment(sketch, "E7.5.0.65", {"start": v(-98.15, 9.9) * mm, "end": v(-97.84, 9.9) * mm});
            skLineSegment(sketch, "E7.5.0.66", {"start": v(-89.75, 9.9) * mm, "end": v(-89.44, 9.9) * mm});
            skLineSegment(sketch, "E7.5.0.67", {"start": v(-94.55, 9.9) * mm, "end": v(-94.24, 9.9) * mm});
            skLineSegment(sketch, "E7.5.0.68", {"start": v(-89.75, 8.93) * mm, "end": v(-89.44, 8.93) * mm});
            skLineSegment(sketch, "E7.5.0.69", {"start": v(-94.55, 8.93) * mm, "end": v(-94.24, 8.93) * mm});
            skLineSegment(sketch, "E7.5.0.70", {"start": v(-75.35, 8.93) * mm, "end": v(-75.04, 8.93) * mm});
            skLineSegment(sketch, "E7.5.0.71", {"start": v(-80.15, 8.93) * mm, "end": v(-79.84, 8.93) * mm});
            skLineSegment(sketch, "E7.5.0.72", {"start": v(-81.35, 9.9) * mm, "end": v(-81.04, 9.9) * mm});
            skLineSegment(sketch, "E7.5.0.73", {"start": v(-88.55, 8.93) * mm, "end": v(-88.24, 8.93) * mm});
            skLineSegment(sketch, "E7.5.0.74", {"start": v(-86.15, 9.9) * mm, "end": v(-85.84, 9.9) * mm});
            skLineSegment(sketch, "E7.5.0.75", {"start": v(-90.95, 9.9) * mm, "end": v(-90.64, 9.9) * mm});
            skLineSegment(sketch, "E7.5.0.76", {"start": v(-93.35, 8.93) * mm, "end": v(-93.04, 8.93) * mm});
            skLineSegment(sketch, "E7.5.0.77", {"start": v(-95.75, 9.9) * mm, "end": v(-95.44, 9.9) * mm});
            skLineSegment(sketch, "E7.5.0.78", {"start": v(-76.55, 9.9) * mm, "end": v(-76.24, 9.9) * mm});
            skLineSegment(sketch, "E7.5.0.79", {"start": v(-88.55, 9.9) * mm, "end": v(-88.24, 9.9) * mm});
            skLineSegment(sketch, "E7.5.0.80", {"start": v(-93.35, 9.9) * mm, "end": v(-93.04, 9.9) * mm});
            skLineSegment(sketch, "E7.5.0.81", {"start": v(-74.15, 9.9) * mm, "end": v(-73.84, 9.9) * mm});
            skLineSegment(sketch, "E7.5.0.82", {"start": v(-78.95, 9.9) * mm, "end": v(-78.64, 9.9) * mm});
            skLineSegment(sketch, "E7.5.0.83", {"start": v(-83.75, 9.9) * mm, "end": v(-83.44, 9.9) * mm});
            skLineSegment(sketch, "E7.5.0.84", {"start": v(-86.15, 8.93) * mm, "end": v(-85.84, 8.93) * mm});
            skLineSegment(sketch, "E7.5.0.85", {"start": v(-88.55, 9.9) * mm, "end": v(-88.55, 8.93) * mm});
            skLineSegment(sketch, "E7.5.0.86", {"start": v(-90.95, 8.93) * mm, "end": v(-90.64, 8.93) * mm});
            skLineSegment(sketch, "E7.5.0.87", {"start": v(-93.35, 9.9) * mm, "end": v(-93.35, 8.93) * mm});
            skLineSegment(sketch, "E7.5.0.88", {"start": v(-95.75, 8.93) * mm, "end": v(-95.44, 8.93) * mm});
            skLineSegment(sketch, "E7.5.0.89", {"start": v(-88.24, 9.9) * mm, "end": v(-88.24, 8.93) * mm});
            skLineSegment(sketch, "E7.5.0.90", {"start": v(-86.15, 9.9) * mm, "end": v(-86.15, 8.93) * mm});
            skLineSegment(sketch, "E7.5.0.91", {"start": v(-93.04, 9.9) * mm, "end": v(-93.04, 8.93) * mm});
            skLineSegment(sketch, "E7.5.0.92", {"start": v(-90.95, 9.9) * mm, "end": v(-90.95, 8.93) * mm});
            skLineSegment(sketch, "E7.5.0.93", {"start": v(-95.75, 9.9) * mm, "end": v(-95.75, 8.93) * mm});
            skLineSegment(sketch, "E7.5.0.94", {"start": v(-90.64, 9.9) * mm, "end": v(-90.64, 8.93) * mm});
            skLineSegment(sketch, "E7.5.0.95", {"start": v(-95.44, 9.9) * mm, "end": v(-95.44, 8.93) * mm});
            skLineSegment(sketch, "E7.5.0.96", {"start": v(-85.84, 9.9) * mm, "end": v(-85.84, 8.93) * mm});
            skLineSegment(sketch, "E7.6.0.0", {"start": v(-101.73, 8.05) * mm, "end": v(-101.73, 7.08) * mm});
            skLineSegment(sketch, "E7.6.0.1", {"start": v(-101.42, 8.05) * mm, "end": v(-101.42, 7.08) * mm});
            skLineSegment(sketch, "E7.6.0.2", {"start": v(-99.33, 8.05) * mm, "end": v(-99.33, 7.08) * mm});
            skLineSegment(sketch, "E7.6.0.3", {"start": v(-99.02, 8.05) * mm, "end": v(-99.02, 7.08) * mm});
            skLineSegment(sketch, "E7.6.0.4", {"start": v(-75.33, 8.05) * mm, "end": v(-75.02, 8.05) * mm});
            skLineSegment(sketch, "E7.6.0.5", {"start": v(-80.13, 8.05) * mm, "end": v(-79.82, 8.05) * mm});
            skLineSegment(sketch, "E7.6.0.6", {"start": v(-84.93, 8.05) * mm, "end": v(-84.62, 8.05) * mm});
            skLineSegment(sketch, "E7.6.0.7", {"start": v(-82.53, 8.05) * mm, "end": v(-82.53, 7.08) * mm});
            skLineSegment(sketch, "E7.6.0.8", {"start": v(-87.33, 8.05) * mm, "end": v(-87.33, 7.08) * mm});
            skLineSegment(sketch, "E7.6.0.9", {"start": v(-92.13, 8.05) * mm, "end": v(-92.13, 7.08) * mm});
            skLineSegment(sketch, "E7.6.0.10", {"start": v(-96.93, 8.05) * mm, "end": v(-96.93, 7.08) * mm});
            skLineSegment(sketch, "E7.6.0.11", {"start": v(-77.73, 8.05) * mm, "end": v(-77.73, 7.08) * mm});
            skLineSegment(sketch, "E7.6.0.12", {"start": v(-84.93, 7.08) * mm, "end": v(-84.62, 7.08) * mm});
            skLineSegment(sketch, "E7.6.0.13", {"start": v(-77.42, 8.05) * mm, "end": v(-77.42, 7.08) * mm});
            skLineSegment(sketch, "E7.6.0.14", {"start": v(-89.73, 8.05) * mm, "end": v(-89.73, 7.08) * mm});
            skLineSegment(sketch, "E7.6.0.15", {"start": v(-94.53, 8.05) * mm, "end": v(-94.53, 7.08) * mm});
            skLineSegment(sketch, "E7.6.0.16", {"start": v(-75.33, 8.05) * mm, "end": v(-75.33, 7.08) * mm});
            skLineSegment(sketch, "E7.6.0.17", {"start": v(-80.13, 8.05) * mm, "end": v(-80.13, 7.08) * mm});
            skLineSegment(sketch, "E7.6.0.18", {"start": v(-84.93, 8.05) * mm, "end": v(-84.93, 7.08) * mm});
            skLineSegment(sketch, "E7.6.0.19", {"start": v(-82.22, 8.05) * mm, "end": v(-82.22, 7.08) * mm});
            skLineSegment(sketch, "E7.6.0.20", {"start": v(-87.02, 8.05) * mm, "end": v(-87.02, 7.08) * mm});
            skLineSegment(sketch, "E7.6.0.21", {"start": v(-91.82, 8.05) * mm, "end": v(-91.82, 7.08) * mm});
            skLineSegment(sketch, "E7.6.0.22", {"start": v(-96.62, 8.05) * mm, "end": v(-96.62, 7.08) * mm});
            skLineSegment(sketch, "E7.6.0.23", {"start": v(-89.42, 8.05) * mm, "end": v(-89.42, 7.08) * mm});
            skLineSegment(sketch, "E7.6.0.24", {"start": v(-94.22, 8.05) * mm, "end": v(-94.22, 7.08) * mm});
            skLineSegment(sketch, "E7.6.0.25", {"start": v(-75.02, 8.05) * mm, "end": v(-75.02, 7.08) * mm});
            skLineSegment(sketch, "E7.6.0.26", {"start": v(-79.82, 8.05) * mm, "end": v(-79.82, 7.08) * mm});
            skLineSegment(sketch, "E7.6.0.27", {"start": v(-84.62, 8.05) * mm, "end": v(-84.62, 7.08) * mm});
            skLineSegment(sketch, "E7.6.0.28", {"start": v(-83.73, 7.08) * mm, "end": v(-83.42, 7.08) * mm});
            skLineSegment(sketch, "E7.6.0.29", {"start": v(-74.13, 7.08) * mm, "end": v(-73.82, 7.08) * mm});
            skLineSegment(sketch, "E7.6.0.30", {"start": v(-78.93, 7.08) * mm, "end": v(-78.62, 7.08) * mm});
            skLineSegment(sketch, "E7.6.0.31", {"start": v(-83.73, 8.05) * mm, "end": v(-83.73, 7.08) * mm});
            skLineSegment(sketch, "E7.6.0.32", {"start": v(-81.33, 7.08) * mm, "end": v(-81.02, 7.08) * mm});
            skLineSegment(sketch, "E7.6.0.33", {"start": v(-74.13, 8.05) * mm, "end": v(-74.13, 7.08) * mm});
            skLineSegment(sketch, "E7.6.0.34", {"start": v(-78.93, 8.05) * mm, "end": v(-78.93, 7.08) * mm});
            skLineSegment(sketch, "E7.6.0.35", {"start": v(-76.53, 7.08) * mm, "end": v(-76.22, 7.08) * mm});
            skLineSegment(sketch, "E7.6.0.36", {"start": v(-81.33, 8.05) * mm, "end": v(-81.33, 7.08) * mm});
            skLineSegment(sketch, "E7.6.0.37", {"start": v(-83.42, 8.05) * mm, "end": v(-83.42, 7.08) * mm});
            skLineSegment(sketch, "E7.6.0.38", {"start": v(-73.82, 8.05) * mm, "end": v(-73.82, 7.08) * mm});
            skLineSegment(sketch, "E7.6.0.39", {"start": v(-78.62, 8.05) * mm, "end": v(-78.62, 7.08) * mm});
            skLineSegment(sketch, "E7.6.0.40", {"start": v(-76.53, 8.05) * mm, "end": v(-76.53, 7.08) * mm});
            skLineSegment(sketch, "E7.6.0.41", {"start": v(-82.53, 8.05) * mm, "end": v(-82.22, 8.05) * mm});
            skLineSegment(sketch, "E7.6.0.42", {"start": v(-87.33, 8.05) * mm, "end": v(-87.02, 8.05) * mm});
            skLineSegment(sketch, "E7.6.0.43", {"start": v(-92.13, 8.05) * mm, "end": v(-91.82, 8.05) * mm});
            skLineSegment(sketch, "E7.6.0.44", {"start": v(-96.93, 8.05) * mm, "end": v(-96.62, 8.05) * mm});
            skLineSegment(sketch, "E7.6.0.45", {"start": v(-101.73, 7.08) * mm, "end": v(-100.53, 7.08) * mm, "construction": true});
            skLineSegment(sketch, "E7.6.0.46", {"start": v(-77.73, 8.05) * mm, "end": v(-77.42, 8.05) * mm});
            skLineSegment(sketch, "E7.6.0.47", {"start": v(-76.22, 8.05) * mm, "end": v(-76.22, 7.08) * mm});
            skLineSegment(sketch, "E7.6.0.48", {"start": v(-81.02, 8.05) * mm, "end": v(-81.02, 7.08) * mm});
            skLineSegment(sketch, "E7.6.0.49", {"start": v(-98.13, 7.08) * mm, "end": v(-97.82, 7.08) * mm});
            skLineSegment(sketch, "E7.6.0.50", {"start": v(-96.93, 7.08) * mm, "end": v(-96.62, 7.08) * mm});
            skLineSegment(sketch, "E7.6.0.51", {"start": v(-92.13, 7.08) * mm, "end": v(-91.82, 7.08) * mm});
            skLineSegment(sketch, "E7.6.0.52", {"start": v(-87.33, 7.08) * mm, "end": v(-87.02, 7.08) * mm});
            skLineSegment(sketch, "E7.6.0.53", {"start": v(-82.53, 7.08) * mm, "end": v(-82.22, 7.08) * mm});
            skLineSegment(sketch, "E7.6.0.54", {"start": v(-77.73, 7.08) * mm, "end": v(-77.42, 7.08) * mm});
            skLineSegment(sketch, "E7.6.0.55", {"start": v(-98.13, 8.05) * mm, "end": v(-98.13, 7.08) * mm});
            skLineSegment(sketch, "E7.6.0.56", {"start": v(-97.82, 8.05) * mm, "end": v(-97.82, 7.08) * mm});
            skLineSegment(sketch, "E7.6.0.57", {"start": v(-101.73, 8.05) * mm, "end": v(-101.42, 8.05) * mm});
            skLineSegment(sketch, "E7.6.0.58", {"start": v(-101.73, 7.08) * mm, "end": v(-101.42, 7.08) * mm});
            skLineSegment(sketch, "E7.6.0.59", {"start": v(-100.53, 8.05) * mm, "end": v(-100.22, 8.05) * mm});
            skLineSegment(sketch, "E7.6.0.60", {"start": v(-100.53, 7.08) * mm, "end": v(-100.22, 7.08) * mm});
            skLineSegment(sketch, "E7.6.0.61", {"start": v(-100.53, 8.05) * mm, "end": v(-100.53, 7.08) * mm});
            skLineSegment(sketch, "E7.6.0.62", {"start": v(-100.22, 8.05) * mm, "end": v(-100.22, 7.08) * mm});
            skLineSegment(sketch, "E7.6.0.63", {"start": v(-99.33, 8.05) * mm, "end": v(-99.02, 8.05) * mm});
            skLineSegment(sketch, "E7.6.0.64", {"start": v(-99.33, 7.08) * mm, "end": v(-99.02, 7.08) * mm});
            skLineSegment(sketch, "E7.6.0.65", {"start": v(-98.13, 8.05) * mm, "end": v(-97.82, 8.05) * mm});
            skLineSegment(sketch, "E7.6.0.66", {"start": v(-89.73, 8.05) * mm, "end": v(-89.42, 8.05) * mm});
            skLineSegment(sketch, "E7.6.0.67", {"start": v(-94.53, 8.05) * mm, "end": v(-94.22, 8.05) * mm});
            skLineSegment(sketch, "E7.6.0.68", {"start": v(-89.73, 7.08) * mm, "end": v(-89.42, 7.08) * mm});
            skLineSegment(sketch, "E7.6.0.69", {"start": v(-94.53, 7.08) * mm, "end": v(-94.22, 7.08) * mm});
            skLineSegment(sketch, "E7.6.0.70", {"start": v(-75.33, 7.08) * mm, "end": v(-75.02, 7.08) * mm});
            skLineSegment(sketch, "E7.6.0.71", {"start": v(-80.13, 7.08) * mm, "end": v(-79.82, 7.08) * mm});
            skLineSegment(sketch, "E7.6.0.72", {"start": v(-81.33, 8.05) * mm, "end": v(-81.02, 8.05) * mm});
            skLineSegment(sketch, "E7.6.0.73", {"start": v(-88.53, 7.08) * mm, "end": v(-88.22, 7.08) * mm});
            skLineSegment(sketch, "E7.6.0.74", {"start": v(-86.13, 8.05) * mm, "end": v(-85.82, 8.05) * mm});
            skLineSegment(sketch, "E7.6.0.75", {"start": v(-90.93, 8.05) * mm, "end": v(-90.62, 8.05) * mm});
            skLineSegment(sketch, "E7.6.0.76", {"start": v(-93.33, 7.08) * mm, "end": v(-93.02, 7.08) * mm});
            skLineSegment(sketch, "E7.6.0.77", {"start": v(-95.73, 8.05) * mm, "end": v(-95.42, 8.05) * mm});
            skLineSegment(sketch, "E7.6.0.78", {"start": v(-76.53, 8.05) * mm, "end": v(-76.22, 8.05) * mm});
            skLineSegment(sketch, "E7.6.0.79", {"start": v(-88.53, 8.05) * mm, "end": v(-88.22, 8.05) * mm});
            skLineSegment(sketch, "E7.6.0.80", {"start": v(-93.33, 8.05) * mm, "end": v(-93.02, 8.05) * mm});
            skLineSegment(sketch, "E7.6.0.81", {"start": v(-74.13, 8.05) * mm, "end": v(-73.82, 8.05) * mm});
            skLineSegment(sketch, "E7.6.0.82", {"start": v(-78.93, 8.05) * mm, "end": v(-78.62, 8.05) * mm});
            skLineSegment(sketch, "E7.6.0.83", {"start": v(-83.73, 8.05) * mm, "end": v(-83.42, 8.05) * mm});
            skLineSegment(sketch, "E7.6.0.84", {"start": v(-86.13, 7.08) * mm, "end": v(-85.82, 7.08) * mm});
            skLineSegment(sketch, "E7.6.0.85", {"start": v(-88.53, 8.05) * mm, "end": v(-88.53, 7.08) * mm});
            skLineSegment(sketch, "E7.6.0.86", {"start": v(-90.93, 7.08) * mm, "end": v(-90.62, 7.08) * mm});
            skLineSegment(sketch, "E7.6.0.87", {"start": v(-93.33, 8.05) * mm, "end": v(-93.33, 7.08) * mm});
            skLineSegment(sketch, "E7.6.0.88", {"start": v(-95.73, 7.08) * mm, "end": v(-95.42, 7.08) * mm});
            skLineSegment(sketch, "E7.6.0.89", {"start": v(-88.22, 8.05) * mm, "end": v(-88.22, 7.08) * mm});
            skLineSegment(sketch, "E7.6.0.90", {"start": v(-86.13, 8.05) * mm, "end": v(-86.13, 7.08) * mm});
            skLineSegment(sketch, "E7.6.0.91", {"start": v(-93.02, 8.05) * mm, "end": v(-93.02, 7.08) * mm});
            skLineSegment(sketch, "E7.6.0.92", {"start": v(-90.93, 8.05) * mm, "end": v(-90.93, 7.08) * mm});
            skLineSegment(sketch, "E7.6.0.93", {"start": v(-95.73, 8.05) * mm, "end": v(-95.73, 7.08) * mm});
            skLineSegment(sketch, "E7.6.0.94", {"start": v(-90.62, 8.05) * mm, "end": v(-90.62, 7.08) * mm});
            skLineSegment(sketch, "E7.6.0.95", {"start": v(-95.42, 8.05) * mm, "end": v(-95.42, 7.08) * mm});
            skLineSegment(sketch, "E7.6.0.96", {"start": v(-85.82, 8.05) * mm, "end": v(-85.82, 7.08) * mm});
            skLineSegment(sketch, "E7.7.0.0", {"start": v(-101.71, 6.2) * mm, "end": v(-101.71, 5.24) * mm});
            skLineSegment(sketch, "E7.7.0.1", {"start": v(-101.4, 6.2) * mm, "end": v(-101.4, 5.24) * mm});
            skLineSegment(sketch, "E7.7.0.2", {"start": v(-99.31, 6.2) * mm, "end": v(-99.31, 5.24) * mm});
            skLineSegment(sketch, "E7.7.0.3", {"start": v(-99, 6.2) * mm, "end": v(-99, 5.24) * mm});
            skLineSegment(sketch, "E7.7.0.4", {"start": v(-75.31, 6.2) * mm, "end": v(-75, 6.2) * mm});
            skLineSegment(sketch, "E7.7.0.5", {"start": v(-80.11, 6.2) * mm, "end": v(-79.8, 6.2) * mm});
            skLineSegment(sketch, "E7.7.0.6", {"start": v(-84.91, 6.2) * mm, "end": v(-84.6, 6.2) * mm});
            skLineSegment(sketch, "E7.7.0.7", {"start": v(-82.51, 6.2) * mm, "end": v(-82.51, 5.24) * mm});
            skLineSegment(sketch, "E7.7.0.8", {"start": v(-87.31, 6.2) * mm, "end": v(-87.31, 5.24) * mm});
            skLineSegment(sketch, "E7.7.0.9", {"start": v(-92.11, 6.2) * mm, "end": v(-92.11, 5.24) * mm});
            skLineSegment(sketch, "E7.7.0.10", {"start": v(-96.91, 6.2) * mm, "end": v(-96.91, 5.24) * mm});
            skLineSegment(sketch, "E7.7.0.11", {"start": v(-77.71, 6.2) * mm, "end": v(-77.71, 5.24) * mm});
            skLineSegment(sketch, "E7.7.0.12", {"start": v(-84.91, 5.24) * mm, "end": v(-84.6, 5.24) * mm});
            skLineSegment(sketch, "E7.7.0.13", {"start": v(-77.4, 6.2) * mm, "end": v(-77.4, 5.24) * mm});
            skLineSegment(sketch, "E7.7.0.14", {"start": v(-89.71, 6.2) * mm, "end": v(-89.71, 5.24) * mm});
            skLineSegment(sketch, "E7.7.0.15", {"start": v(-94.51, 6.2) * mm, "end": v(-94.51, 5.24) * mm});
            skLineSegment(sketch, "E7.7.0.16", {"start": v(-75.31, 6.2) * mm, "end": v(-75.31, 5.24) * mm});
            skLineSegment(sketch, "E7.7.0.17", {"start": v(-80.11, 6.2) * mm, "end": v(-80.11, 5.24) * mm});
            skLineSegment(sketch, "E7.7.0.18", {"start": v(-84.91, 6.2) * mm, "end": v(-84.91, 5.24) * mm});
            skLineSegment(sketch, "E7.7.0.19", {"start": v(-82.2, 6.2) * mm, "end": v(-82.2, 5.24) * mm});
            skLineSegment(sketch, "E7.7.0.20", {"start": v(-87, 6.2) * mm, "end": v(-87, 5.24) * mm});
            skLineSegment(sketch, "E7.7.0.21", {"start": v(-91.8, 6.2) * mm, "end": v(-91.8, 5.24) * mm});
            skLineSegment(sketch, "E7.7.0.22", {"start": v(-96.6, 6.2) * mm, "end": v(-96.6, 5.24) * mm});
            skLineSegment(sketch, "E7.7.0.23", {"start": v(-89.4, 6.2) * mm, "end": v(-89.4, 5.24) * mm});
            skLineSegment(sketch, "E7.7.0.24", {"start": v(-94.2, 6.2) * mm, "end": v(-94.2, 5.24) * mm});
            skLineSegment(sketch, "E7.7.0.25", {"start": v(-75, 6.2) * mm, "end": v(-75, 5.24) * mm});
            skLineSegment(sketch, "E7.7.0.26", {"start": v(-79.8, 6.2) * mm, "end": v(-79.8, 5.24) * mm});
            skLineSegment(sketch, "E7.7.0.27", {"start": v(-84.6, 6.2) * mm, "end": v(-84.6, 5.24) * mm});
            skLineSegment(sketch, "E7.7.0.28", {"start": v(-83.71, 5.24) * mm, "end": v(-83.4, 5.24) * mm});
            skLineSegment(sketch, "E7.7.0.29", {"start": v(-74.11, 5.24) * mm, "end": v(-73.8, 5.24) * mm});
            skLineSegment(sketch, "E7.7.0.30", {"start": v(-78.91, 5.24) * mm, "end": v(-78.6, 5.24) * mm});
            skLineSegment(sketch, "E7.7.0.31", {"start": v(-83.71, 6.2) * mm, "end": v(-83.71, 5.24) * mm});
            skLineSegment(sketch, "E7.7.0.32", {"start": v(-81.31, 5.24) * mm, "end": v(-81, 5.24) * mm});
            skLineSegment(sketch, "E7.7.0.33", {"start": v(-74.11, 6.2) * mm, "end": v(-74.11, 5.24) * mm});
            skLineSegment(sketch, "E7.7.0.34", {"start": v(-78.91, 6.2) * mm, "end": v(-78.91, 5.24) * mm});
            skLineSegment(sketch, "E7.7.0.35", {"start": v(-76.51, 5.24) * mm, "end": v(-76.2, 5.24) * mm});
            skLineSegment(sketch, "E7.7.0.36", {"start": v(-81.31, 6.2) * mm, "end": v(-81.31, 5.24) * mm});
            skLineSegment(sketch, "E7.7.0.37", {"start": v(-83.4, 6.2) * mm, "end": v(-83.4, 5.24) * mm});
            skLineSegment(sketch, "E7.7.0.38", {"start": v(-73.8, 6.2) * mm, "end": v(-73.8, 5.24) * mm});
            skLineSegment(sketch, "E7.7.0.39", {"start": v(-78.6, 6.2) * mm, "end": v(-78.6, 5.24) * mm});
            skLineSegment(sketch, "E7.7.0.40", {"start": v(-76.51, 6.2) * mm, "end": v(-76.51, 5.24) * mm});
            skLineSegment(sketch, "E7.7.0.41", {"start": v(-82.51, 6.2) * mm, "end": v(-82.2, 6.2) * mm});
            skLineSegment(sketch, "E7.7.0.42", {"start": v(-87.31, 6.2) * mm, "end": v(-87, 6.2) * mm});
            skLineSegment(sketch, "E7.7.0.43", {"start": v(-92.11, 6.2) * mm, "end": v(-91.8, 6.2) * mm});
            skLineSegment(sketch, "E7.7.0.44", {"start": v(-96.91, 6.2) * mm, "end": v(-96.6, 6.2) * mm});
            skLineSegment(sketch, "E7.7.0.45", {"start": v(-101.71, 5.24) * mm, "end": v(-100.51, 5.24) * mm, "construction": true});
            skLineSegment(sketch, "E7.7.0.46", {"start": v(-77.71, 6.2) * mm, "end": v(-77.4, 6.2) * mm});
            skLineSegment(sketch, "E7.7.0.47", {"start": v(-76.2, 6.2) * mm, "end": v(-76.2, 5.24) * mm});
            skLineSegment(sketch, "E7.7.0.48", {"start": v(-81, 6.2) * mm, "end": v(-81, 5.24) * mm});
            skLineSegment(sketch, "E7.7.0.49", {"start": v(-98.11, 5.24) * mm, "end": v(-97.8, 5.24) * mm});
            skLineSegment(sketch, "E7.7.0.50", {"start": v(-96.91, 5.24) * mm, "end": v(-96.6, 5.24) * mm});
            skLineSegment(sketch, "E7.7.0.51", {"start": v(-92.11, 5.24) * mm, "end": v(-91.8, 5.24) * mm});
            skLineSegment(sketch, "E7.7.0.52", {"start": v(-87.31, 5.24) * mm, "end": v(-87, 5.24) * mm});
            skLineSegment(sketch, "E7.7.0.53", {"start": v(-82.51, 5.24) * mm, "end": v(-82.2, 5.24) * mm});
            skLineSegment(sketch, "E7.7.0.54", {"start": v(-77.71, 5.24) * mm, "end": v(-77.4, 5.24) * mm});
            skLineSegment(sketch, "E7.7.0.55", {"start": v(-98.11, 6.2) * mm, "end": v(-98.11, 5.24) * mm});
            skLineSegment(sketch, "E7.7.0.56", {"start": v(-97.8, 6.2) * mm, "end": v(-97.8, 5.24) * mm});
            skLineSegment(sketch, "E7.7.0.57", {"start": v(-101.71, 6.2) * mm, "end": v(-101.4, 6.2) * mm});
            skLineSegment(sketch, "E7.7.0.58", {"start": v(-101.71, 5.24) * mm, "end": v(-101.4, 5.24) * mm});
            skLineSegment(sketch, "E7.7.0.59", {"start": v(-100.51, 6.2) * mm, "end": v(-100.2, 6.2) * mm});
            skLineSegment(sketch, "E7.7.0.60", {"start": v(-100.51, 5.24) * mm, "end": v(-100.2, 5.24) * mm});
            skLineSegment(sketch, "E7.7.0.61", {"start": v(-100.51, 6.2) * mm, "end": v(-100.51, 5.24) * mm});
            skLineSegment(sketch, "E7.7.0.62", {"start": v(-100.2, 6.2) * mm, "end": v(-100.2, 5.24) * mm});
            skLineSegment(sketch, "E7.7.0.63", {"start": v(-99.31, 6.2) * mm, "end": v(-99, 6.2) * mm});
            skLineSegment(sketch, "E7.7.0.64", {"start": v(-99.31, 5.24) * mm, "end": v(-99, 5.24) * mm});
            skLineSegment(sketch, "E7.7.0.65", {"start": v(-98.11, 6.2) * mm, "end": v(-97.8, 6.2) * mm});
            skLineSegment(sketch, "E7.7.0.66", {"start": v(-89.71, 6.2) * mm, "end": v(-89.4, 6.2) * mm});
            skLineSegment(sketch, "E7.7.0.67", {"start": v(-94.51, 6.2) * mm, "end": v(-94.2, 6.2) * mm});
            skLineSegment(sketch, "E7.7.0.68", {"start": v(-89.71, 5.24) * mm, "end": v(-89.4, 5.24) * mm});
            skLineSegment(sketch, "E7.7.0.69", {"start": v(-94.51, 5.24) * mm, "end": v(-94.2, 5.24) * mm});
            skLineSegment(sketch, "E7.7.0.70", {"start": v(-75.31, 5.24) * mm, "end": v(-75, 5.24) * mm});
            skLineSegment(sketch, "E7.7.0.71", {"start": v(-80.11, 5.24) * mm, "end": v(-79.8, 5.24) * mm});
            skLineSegment(sketch, "E7.7.0.72", {"start": v(-81.31, 6.2) * mm, "end": v(-81, 6.2) * mm});
            skLineSegment(sketch, "E7.7.0.73", {"start": v(-88.51, 5.24) * mm, "end": v(-88.2, 5.24) * mm});
            skLineSegment(sketch, "E7.7.0.74", {"start": v(-86.11, 6.2) * mm, "end": v(-85.8, 6.2) * mm});
            skLineSegment(sketch, "E7.7.0.75", {"start": v(-90.91, 6.2) * mm, "end": v(-90.6, 6.2) * mm});
            skLineSegment(sketch, "E7.7.0.76", {"start": v(-93.31, 5.24) * mm, "end": v(-93, 5.24) * mm});
            skLineSegment(sketch, "E7.7.0.77", {"start": v(-95.71, 6.2) * mm, "end": v(-95.4, 6.2) * mm});
            skLineSegment(sketch, "E7.7.0.78", {"start": v(-76.51, 6.2) * mm, "end": v(-76.2, 6.2) * mm});
            skLineSegment(sketch, "E7.7.0.79", {"start": v(-88.51, 6.2) * mm, "end": v(-88.2, 6.2) * mm});
            skLineSegment(sketch, "E7.7.0.80", {"start": v(-93.31, 6.2) * mm, "end": v(-93, 6.2) * mm});
            skLineSegment(sketch, "E7.7.0.81", {"start": v(-74.11, 6.2) * mm, "end": v(-73.8, 6.2) * mm});
            skLineSegment(sketch, "E7.7.0.82", {"start": v(-78.91, 6.2) * mm, "end": v(-78.6, 6.2) * mm});
            skLineSegment(sketch, "E7.7.0.83", {"start": v(-83.71, 6.2) * mm, "end": v(-83.4, 6.2) * mm});
            skLineSegment(sketch, "E7.7.0.84", {"start": v(-86.11, 5.24) * mm, "end": v(-85.8, 5.24) * mm});
            skLineSegment(sketch, "E7.7.0.85", {"start": v(-88.51, 6.2) * mm, "end": v(-88.51, 5.24) * mm});
            skLineSegment(sketch, "E7.7.0.86", {"start": v(-90.91, 5.24) * mm, "end": v(-90.6, 5.24) * mm});
            skLineSegment(sketch, "E7.7.0.87", {"start": v(-93.31, 6.2) * mm, "end": v(-93.31, 5.24) * mm});
            skLineSegment(sketch, "E7.7.0.88", {"start": v(-95.71, 5.24) * mm, "end": v(-95.4, 5.24) * mm});
            skLineSegment(sketch, "E7.7.0.89", {"start": v(-88.2, 6.2) * mm, "end": v(-88.2, 5.24) * mm});
            skLineSegment(sketch, "E7.7.0.90", {"start": v(-86.11, 6.2) * mm, "end": v(-86.11, 5.24) * mm});
            skLineSegment(sketch, "E7.7.0.91", {"start": v(-93, 6.2) * mm, "end": v(-93, 5.24) * mm});
            skLineSegment(sketch, "E7.7.0.92", {"start": v(-90.91, 6.2) * mm, "end": v(-90.91, 5.24) * mm});
            skLineSegment(sketch, "E7.7.0.93", {"start": v(-95.71, 6.2) * mm, "end": v(-95.71, 5.24) * mm});
            skLineSegment(sketch, "E7.7.0.94", {"start": v(-90.6, 6.2) * mm, "end": v(-90.6, 5.24) * mm});
            skLineSegment(sketch, "E7.7.0.95", {"start": v(-95.4, 6.2) * mm, "end": v(-95.4, 5.24) * mm});
            skLineSegment(sketch, "E7.7.0.96", {"start": v(-85.8, 6.2) * mm, "end": v(-85.8, 5.24) * mm});
            skLineSegment(sketch, "E7.8.0.0", {"start": v(-101.7, 4.36) * mm, "end": v(-101.7, 3.4) * mm});
            skLineSegment(sketch, "E7.8.0.1", {"start": v(-101.39, 4.36) * mm, "end": v(-101.39, 3.4) * mm});
            skLineSegment(sketch, "E7.8.0.2", {"start": v(-99.3, 4.36) * mm, "end": v(-99.3, 3.4) * mm});
            skLineSegment(sketch, "E7.8.0.3", {"start": v(-98.99, 4.36) * mm, "end": v(-98.99, 3.4) * mm});
            skLineSegment(sketch, "E7.8.0.4", {"start": v(-75.3, 4.36) * mm, "end": v(-74.99, 4.36) * mm});
            skLineSegment(sketch, "E7.8.0.5", {"start": v(-80.1, 4.36) * mm, "end": v(-79.79, 4.36) * mm});
            skLineSegment(sketch, "E7.8.0.6", {"start": v(-84.9, 4.36) * mm, "end": v(-84.59, 4.36) * mm});
            skLineSegment(sketch, "E7.8.0.7", {"start": v(-82.5, 4.36) * mm, "end": v(-82.5, 3.4) * mm});
            skLineSegment(sketch, "E7.8.0.8", {"start": v(-87.3, 4.36) * mm, "end": v(-87.3, 3.4) * mm});
            skLineSegment(sketch, "E7.8.0.9", {"start": v(-92.1, 4.36) * mm, "end": v(-92.1, 3.4) * mm});
            skLineSegment(sketch, "E7.8.0.10", {"start": v(-96.9, 4.36) * mm, "end": v(-96.9, 3.4) * mm});
            skLineSegment(sketch, "E7.8.0.11", {"start": v(-77.7, 4.36) * mm, "end": v(-77.7, 3.4) * mm});
            skLineSegment(sketch, "E7.8.0.12", {"start": v(-84.9, 3.4) * mm, "end": v(-84.59, 3.4) * mm});
            skLineSegment(sketch, "E7.8.0.13", {"start": v(-77.39, 4.36) * mm, "end": v(-77.39, 3.4) * mm});
            skLineSegment(sketch, "E7.8.0.14", {"start": v(-89.7, 4.36) * mm, "end": v(-89.7, 3.4) * mm});
            skLineSegment(sketch, "E7.8.0.15", {"start": v(-94.5, 4.36) * mm, "end": v(-94.5, 3.4) * mm});
            skLineSegment(sketch, "E7.8.0.16", {"start": v(-75.3, 4.36) * mm, "end": v(-75.3, 3.4) * mm});
            skLineSegment(sketch, "E7.8.0.17", {"start": v(-80.1, 4.36) * mm, "end": v(-80.1, 3.4) * mm});
            skLineSegment(sketch, "E7.8.0.18", {"start": v(-84.9, 4.36) * mm, "end": v(-84.9, 3.4) * mm});
            skLineSegment(sketch, "E7.8.0.19", {"start": v(-82.19, 4.36) * mm, "end": v(-82.19, 3.4) * mm});
            skLineSegment(sketch, "E7.8.0.20", {"start": v(-86.99, 4.36) * mm, "end": v(-86.99, 3.4) * mm});
            skLineSegment(sketch, "E7.8.0.21", {"start": v(-91.79, 4.36) * mm, "end": v(-91.79, 3.4) * mm});
            skLineSegment(sketch, "E7.8.0.22", {"start": v(-96.59, 4.36) * mm, "end": v(-96.59, 3.4) * mm});
            skLineSegment(sketch, "E7.8.0.23", {"start": v(-89.39, 4.36) * mm, "end": v(-89.39, 3.4) * mm});
            skLineSegment(sketch, "E7.8.0.24", {"start": v(-94.19, 4.36) * mm, "end": v(-94.19, 3.4) * mm});
            skLineSegment(sketch, "E7.8.0.25", {"start": v(-74.99, 4.36) * mm, "end": v(-74.99, 3.4) * mm});
            skLineSegment(sketch, "E7.8.0.26", {"start": v(-79.79, 4.36) * mm, "end": v(-79.79, 3.4) * mm});
            skLineSegment(sketch, "E7.8.0.27", {"start": v(-84.59, 4.36) * mm, "end": v(-84.59, 3.4) * mm});
            skLineSegment(sketch, "E7.8.0.28", {"start": v(-83.7, 3.4) * mm, "end": v(-83.39, 3.4) * mm});
            skLineSegment(sketch, "E7.8.0.29", {"start": v(-74.1, 3.4) * mm, "end": v(-73.79, 3.4) * mm});
            skLineSegment(sketch, "E7.8.0.30", {"start": v(-78.9, 3.4) * mm, "end": v(-78.59, 3.4) * mm});
            skLineSegment(sketch, "E7.8.0.31", {"start": v(-83.7, 4.36) * mm, "end": v(-83.7, 3.4) * mm});
            skLineSegment(sketch, "E7.8.0.32", {"start": v(-81.3, 3.4) * mm, "end": v(-80.99, 3.4) * mm});
            skLineSegment(sketch, "E7.8.0.33", {"start": v(-74.1, 4.36) * mm, "end": v(-74.1, 3.4) * mm});
            skLineSegment(sketch, "E7.8.0.34", {"start": v(-78.9, 4.36) * mm, "end": v(-78.9, 3.4) * mm});
            skLineSegment(sketch, "E7.8.0.35", {"start": v(-76.5, 3.4) * mm, "end": v(-76.19, 3.4) * mm});
            skLineSegment(sketch, "E7.8.0.36", {"start": v(-81.3, 4.36) * mm, "end": v(-81.3, 3.4) * mm});
            skLineSegment(sketch, "E7.8.0.37", {"start": v(-83.39, 4.36) * mm, "end": v(-83.39, 3.4) * mm});
            skLineSegment(sketch, "E7.8.0.38", {"start": v(-73.79, 4.36) * mm, "end": v(-73.79, 3.4) * mm});
            skLineSegment(sketch, "E7.8.0.39", {"start": v(-78.59, 4.36) * mm, "end": v(-78.59, 3.4) * mm});
            skLineSegment(sketch, "E7.8.0.40", {"start": v(-76.5, 4.36) * mm, "end": v(-76.5, 3.4) * mm});
            skLineSegment(sketch, "E7.8.0.41", {"start": v(-82.5, 4.36) * mm, "end": v(-82.19, 4.36) * mm});
            skLineSegment(sketch, "E7.8.0.42", {"start": v(-87.3, 4.36) * mm, "end": v(-86.99, 4.36) * mm});
            skLineSegment(sketch, "E7.8.0.43", {"start": v(-92.1, 4.36) * mm, "end": v(-91.79, 4.36) * mm});
            skLineSegment(sketch, "E7.8.0.44", {"start": v(-96.9, 4.36) * mm, "end": v(-96.59, 4.36) * mm});
            skLineSegment(sketch, "E7.8.0.45", {"start": v(-101.7, 3.4) * mm, "end": v(-100.5, 3.4) * mm, "construction": true});
            skLineSegment(sketch, "E7.8.0.46", {"start": v(-77.7, 4.36) * mm, "end": v(-77.39, 4.36) * mm});
            skLineSegment(sketch, "E7.8.0.47", {"start": v(-76.19, 4.36) * mm, "end": v(-76.19, 3.4) * mm});
            skLineSegment(sketch, "E7.8.0.48", {"start": v(-80.99, 4.36) * mm, "end": v(-80.99, 3.4) * mm});
            skLineSegment(sketch, "E7.8.0.49", {"start": v(-98.1, 3.4) * mm, "end": v(-97.79, 3.4) * mm});
            skLineSegment(sketch, "E7.8.0.50", {"start": v(-96.9, 3.4) * mm, "end": v(-96.59, 3.4) * mm});
            skLineSegment(sketch, "E7.8.0.51", {"start": v(-92.1, 3.4) * mm, "end": v(-91.79, 3.4) * mm});
            skLineSegment(sketch, "E7.8.0.52", {"start": v(-87.3, 3.4) * mm, "end": v(-86.99, 3.4) * mm});
            skLineSegment(sketch, "E7.8.0.53", {"start": v(-82.5, 3.4) * mm, "end": v(-82.19, 3.4) * mm});
            skLineSegment(sketch, "E7.8.0.54", {"start": v(-77.7, 3.4) * mm, "end": v(-77.39, 3.4) * mm});
            skLineSegment(sketch, "E7.8.0.55", {"start": v(-98.1, 4.36) * mm, "end": v(-98.1, 3.4) * mm});
            skLineSegment(sketch, "E7.8.0.56", {"start": v(-97.79, 4.36) * mm, "end": v(-97.79, 3.4) * mm});
            skLineSegment(sketch, "E7.8.0.57", {"start": v(-101.7, 4.36) * mm, "end": v(-101.39, 4.36) * mm});
            skLineSegment(sketch, "E7.8.0.58", {"start": v(-101.7, 3.4) * mm, "end": v(-101.39, 3.4) * mm});
            skLineSegment(sketch, "E7.8.0.59", {"start": v(-100.5, 4.36) * mm, "end": v(-100.19, 4.36) * mm});
            skLineSegment(sketch, "E7.8.0.60", {"start": v(-100.5, 3.4) * mm, "end": v(-100.19, 3.4) * mm});
            skLineSegment(sketch, "E7.8.0.61", {"start": v(-100.5, 4.36) * mm, "end": v(-100.5, 3.4) * mm});
            skLineSegment(sketch, "E7.8.0.62", {"start": v(-100.19, 4.36) * mm, "end": v(-100.19, 3.4) * mm});
            skLineSegment(sketch, "E7.8.0.63", {"start": v(-99.3, 4.36) * mm, "end": v(-98.99, 4.36) * mm});
            skLineSegment(sketch, "E7.8.0.64", {"start": v(-99.3, 3.4) * mm, "end": v(-98.99, 3.4) * mm});
            skLineSegment(sketch, "E7.8.0.65", {"start": v(-98.1, 4.36) * mm, "end": v(-97.79, 4.36) * mm});
            skLineSegment(sketch, "E7.8.0.66", {"start": v(-89.7, 4.36) * mm, "end": v(-89.39, 4.36) * mm});
            skLineSegment(sketch, "E7.8.0.67", {"start": v(-94.5, 4.36) * mm, "end": v(-94.19, 4.36) * mm});
            skLineSegment(sketch, "E7.8.0.68", {"start": v(-89.7, 3.4) * mm, "end": v(-89.39, 3.4) * mm});
            skLineSegment(sketch, "E7.8.0.69", {"start": v(-94.5, 3.4) * mm, "end": v(-94.19, 3.4) * mm});
            skLineSegment(sketch, "E7.8.0.70", {"start": v(-75.3, 3.4) * mm, "end": v(-74.99, 3.4) * mm});
            skLineSegment(sketch, "E7.8.0.71", {"start": v(-80.1, 3.4) * mm, "end": v(-79.79, 3.4) * mm});
            skLineSegment(sketch, "E7.8.0.72", {"start": v(-81.3, 4.36) * mm, "end": v(-80.99, 4.36) * mm});
            skLineSegment(sketch, "E7.8.0.73", {"start": v(-88.5, 3.4) * mm, "end": v(-88.19, 3.4) * mm});
            skLineSegment(sketch, "E7.8.0.74", {"start": v(-86.1, 4.36) * mm, "end": v(-85.79, 4.36) * mm});
            skLineSegment(sketch, "E7.8.0.75", {"start": v(-90.9, 4.36) * mm, "end": v(-90.59, 4.36) * mm});
            skLineSegment(sketch, "E7.8.0.76", {"start": v(-93.3, 3.4) * mm, "end": v(-92.99, 3.4) * mm});
            skLineSegment(sketch, "E7.8.0.77", {"start": v(-95.7, 4.36) * mm, "end": v(-95.39, 4.36) * mm});
            skLineSegment(sketch, "E7.8.0.78", {"start": v(-76.5, 4.36) * mm, "end": v(-76.19, 4.36) * mm});
            skLineSegment(sketch, "E7.8.0.79", {"start": v(-88.5, 4.36) * mm, "end": v(-88.19, 4.36) * mm});
            skLineSegment(sketch, "E7.8.0.80", {"start": v(-93.3, 4.36) * mm, "end": v(-92.99, 4.36) * mm});
            skLineSegment(sketch, "E7.8.0.81", {"start": v(-74.1, 4.36) * mm, "end": v(-73.79, 4.36) * mm});
            skLineSegment(sketch, "E7.8.0.82", {"start": v(-78.9, 4.36) * mm, "end": v(-78.59, 4.36) * mm});
            skLineSegment(sketch, "E7.8.0.83", {"start": v(-83.7, 4.36) * mm, "end": v(-83.39, 4.36) * mm});
            skLineSegment(sketch, "E7.8.0.84", {"start": v(-86.1, 3.4) * mm, "end": v(-85.79, 3.4) * mm});
            skLineSegment(sketch, "E7.8.0.85", {"start": v(-88.5, 4.36) * mm, "end": v(-88.5, 3.4) * mm});
            skLineSegment(sketch, "E7.8.0.86", {"start": v(-90.9, 3.4) * mm, "end": v(-90.59, 3.4) * mm});
            skLineSegment(sketch, "E7.8.0.87", {"start": v(-93.3, 4.36) * mm, "end": v(-93.3, 3.4) * mm});
            skLineSegment(sketch, "E7.8.0.88", {"start": v(-95.7, 3.4) * mm, "end": v(-95.39, 3.4) * mm});
            skLineSegment(sketch, "E7.8.0.89", {"start": v(-88.19, 4.36) * mm, "end": v(-88.19, 3.4) * mm});
            skLineSegment(sketch, "E7.8.0.90", {"start": v(-86.1, 4.36) * mm, "end": v(-86.1, 3.4) * mm});
            skLineSegment(sketch, "E7.8.0.91", {"start": v(-92.99, 4.36) * mm, "end": v(-92.99, 3.4) * mm});
            skLineSegment(sketch, "E7.8.0.92", {"start": v(-90.9, 4.36) * mm, "end": v(-90.9, 3.4) * mm});
            skLineSegment(sketch, "E7.8.0.93", {"start": v(-95.7, 4.36) * mm, "end": v(-95.7, 3.4) * mm});
            skLineSegment(sketch, "E7.8.0.94", {"start": v(-90.59, 4.36) * mm, "end": v(-90.59, 3.4) * mm});
            skLineSegment(sketch, "E7.8.0.95", {"start": v(-95.39, 4.36) * mm, "end": v(-95.39, 3.4) * mm});
            skLineSegment(sketch, "E7.8.0.96", {"start": v(-85.79, 4.36) * mm, "end": v(-85.79, 3.4) * mm});
            skLineSegment(sketch, "E7.direction1", {"start": v(-101.84, 18.16) * mm, "end": v(-101.82, 16.31) * mm, "construction": true});
            skSolve(sketch);
        }
        {
            var Q0;
            Q0 = qSketchRegion(id + "F7", true);
            extrude(context, id + "F8", {"entities" : qUnion([Q0]), "operationType" : NewBodyOperationType.ADD, "depth" : 6.5 * mm});
        }
    });
